FCSTD DOCUMENT  (FreeCAD 0.19R)
Label: drive_side_x-axis
License: All rights reserved
LicenseURL: http://en.wikipedia.org/wiki/All_rights_reserved
objects: App::Link×20, App::DocumentObjectGroup×3, PartDesign::CoordinateSystem×1, App::FeaturePython×1, App::Part×1
note: 1 computed .brp shape members not serialized (recipe doc carries the construction recipe); baked Part::Feature solids carry a one-line shape summary decoded from their .brp
EXTERNAL_REF file=angle_machined_2in_25_drive_side.FCStd obj=Local_CS010
EXTERNAL_REF file=bracket_nema_17.FCStd obj=Local_CS004
EXTERNAL_REF file=bracket_nema_17.FCStd obj=Body
EXTERNAL_REF file=bracket_nema_17.FCStd obj=Local_CS001
EXTERNAL_REF file=motor stepper 17hs4401s.FCStd obj=Local_CS
EXTERNAL_REF file=motor stepper 17hs4401s.FCStd obj=Body
EXTERNAL_REF file=coupling_8mm_5mm.FCStd obj=Local_CS
EXTERNAL_REF file=coupling_8mm_5mm.FCStd obj=Body
EXTERNAL_REF file=angle_machined_2in_25_drive_side.FCStd obj=Local_CS007
EXTERNAL_REF file=angle_machined_2in_25_drive_side.FCStd obj=Body
EXTERNAL_REF file=KFL08_bushing.FCStd obj=Local_CS001
EXTERNAL_REF file=KFL08_bushing.FCStd obj=Body
EXTERNAL_REF file=angle_machined_2in_25_drive_side.FCStd obj=Local_CS021
EXTERNAL_REF file=support_shaft_horiz_8mm.FCStd obj=Local_CS003
EXTERNAL_REF file=support_shaft_horiz_8mm.FCStd obj=Body
EXTERNAL_REF file=angle_machined_2in_25_drive_side.FCStd obj=Local_CS019
EXTERNAL_REF file=support_shaft_horiz_8mm.FCStd obj=Local_CS002
EXTERNAL_REF file=angle_machined_2in_25_drive_side.FCStd obj=Local_CS009
EXTERNAL_REF file=bearing_linear_8mm_horiz.FCStd obj=Local_CS
EXTERNAL_REF file=bearing_linear_8mm_horiz.FCStd obj=Body
EXTERNAL_REF file=angle_machined_2in_25_drive_side.FCStd obj=Local_CS
EXTERNAL_REF file=bearing_linear_8mm_horiz.FCStd obj=Local_CS004
EXTERNAL_REF file=shaft_8mm.FCStd obj=Local_CS
EXTERNAL_REF file=support_shaft_horiz_8mm.FCStd obj=Local_CS001
EXTERNAL_REF file=shaft_8mm.FCStd obj=Body
EXTERNAL_REF file=support_shaft_horiz_8mm.FCStd obj=Local_CS005
EXTERNAL_REF file=shaft_8mm.FCStd obj=Local_CS001
EXTERNAL_REF file=bearing_linear_8mm_horiz.FCStd obj=Local_CS003
EXTERNAL_REF file=bearing_linear_8mm_horiz.FCStd obj=Local_CS001
EXTERNAL_REF file=coupling_8mm_5mm.FCStd obj=Local_CS001
EXTERNAL_REF file=rod_threaded_8mm.FCStd obj=Local_CS001
EXTERNAL_REF file=rod_threaded_8mm.FCStd obj=Body
EXTERNAL_REF file=angle_machined_2in_25_drive_side.FCStd obj=Local_CS025
EXTERNAL_REF file=nut_angle.FCStd obj=Local_CS
EXTERNAL_REF file=nut_angle.FCStd obj=Body
EXTERNAL_REF file=nut_angle.FCStd obj=Local_CS001
EXTERNAL_REF file=nut_lead_screw_tr8x4.FCStd obj=Local_CS002
EXTERNAL_REF file=nut_lead_screw_tr8x4.FCStd obj=Body

FEATURE [App::DocumentObjectGroup] Parts
FEATURE [PartDesign::CoordinateSystem] LCS_Origin
  AttacherType = Attacher::AttachEngine3D
  MapMode = 2
  Support = -> [X_Axis]
FEATURE [App::FeaturePython] Variables  # WARN: FeaturePython — macro-defined, semantics opaque (R4)
  Type = App::PropertyContainer
FEATURE [App::DocumentObjectGroup] Constraints
FEATURE [App::DocumentObjectGroup] Configurations
FEATURE [App::Link] Body  label="bracket_nema_17"
  AttachedBy = #Local_CS004
  AttachedTo = Body003#Local_CS010
  AttachmentOffset = pos=(0,23,6.35) rot=(0,0,-1;4.71239rad)
  LinkPlacement = pos=(0.015,-4.15,-55.5) rot=(0,0,-1;3.14159rad)
  LinkedObject = -> <external bracket_nema_17.FCStd>#Body
  Placement = pos=(0.015,-4.15,-55.5) rot=(0,0,-1;3.14159rad)
  SolverId = Placement::ExpressionEngine
  expr: Placement = Body003.Placement * angle_machined_2in_25_drive_side#Local_CS010.Placement * AttachmentOffset * bracket_nema_17#Local_CS004.Placement ^ -1
FEATURE [App::Link] Body001  label="motor_nema"
  AttachedBy = #Local_CS
  AttachedTo = Body#Local_CS001
  AttachmentOffset = pos=(0,0,0) rot=(0.707107,0.707107,0;3.14159rad)
  LinkPlacement = pos=(0.015,0.35,-93.5) rot=(0,0,1;1.5708rad)
  LinkedObject = -> <external motor stepper 17hs4401s.FCStd>#Body
  Placement = pos=(0.015,0.35,-93.5) rot=(0,0,1;1.5708rad)
  SolverId = Placement::ExpressionEngine
  expr: Placement = Body.Placement * bracket_nema_17#Local_CS001.Placement * AttachmentOffset * motor_stepper_17hs4401s#Local_CS.Placement ^ -1
FEATURE [App::Link] Body002  label="coupling"
  AttachedBy = #Local_CS
  AttachedTo = Body001#Local_CS
  AttachmentOffset = pos=(0,0,-12) rot=(0,0,1;0rad)
  LinkPlacement = pos=(0.015,0.35,-31) rot=(0.707107,0.707107,0;3.14159rad)
  LinkedObject = -> <external coupling_8mm_5mm.FCStd>#Body
  Placement = pos=(0.015,0.35,-31) rot=(0.707107,0.707107,0;3.14159rad)
  SolverId = Placement::ExpressionEngine
  expr: Placement = Body001.Placement * motor_stepper_17hs4401s#Local_CS.Placement * AttachmentOffset * coupling_8mm_5mm#Local_CS.Placement ^ -1
FEATURE [App::Link] Body003  label="angle_machined_2in_25_drive"
  AttachedBy = #Local_CS007
  AttachedTo = Parent Assembly#LCS_Origin
  AttachmentOffset = pos=(0,0,0) rot=(0,1,0;3.14159rad)
  LinkPlacement = pos=(1.03e-14,-39,6.35) rot=(-0.707107,0,0.707107;3.14159rad)
  LinkedObject = -> <external angle_machined_2in_25_drive_side.FCStd>#Body
  Placement = pos=(1.03e-14,-39,6.35) rot=(-0.707107,0,0.707107;3.14159rad)
  SolverId = Placement::ExpressionEngine
  expr: Placement = LCS_Origin.Placement * AttachmentOffset * angle_machined_2in_25_drive_side#Local_CS007.Placement ^ -1
FEATURE [App::Link] Body004  label="bearing_axial1"
  AttachedBy = #Local_CS001
  AttachedTo = Body003#Local_CS007
  AttachmentOffset = pos=(0,0,0) rot=(0,0,1;3.14159rad)
  LinkPlacement = pos=(-3e-15,0,1.8e-15) rot=(0.707107,0.707107,0;3.14159rad)
  LinkedObject = -> <external KFL08_bushing.FCStd>#Body
  Placement = pos=(-3e-15,0,1.8e-15) rot=(0.707107,0.707107,0;3.14159rad)
  SolverId = Placement::ExpressionEngine
  expr: Placement = Body003.Placement * angle_machined_2in_25_drive_side#Local_CS007.Placement * AttachmentOffset * KFL08_bushing#Local_CS001.Placement ^ -1
FEATURE [App::Link] Body005  label="support_shaft_top"
  AttachedBy = #Local_CS003
  AttachedTo = Body003#Local_CS021
  AttachmentOffset = pos=(0,0,0) rot=(0.707107,0.707107,0;3.14159rad)
  LinkPlacement = pos=(40,-25,11.35) rot=(0,0,1;0rad)
  LinkedObject = -> <external support_shaft_horiz_8mm.FCStd>#Body
  Placement = pos=(40,-25,11.35) rot=(0,0,1;0rad)
  SolverId = Placement::ExpressionEngine
  expr: Placement = Body003.Placement * angle_machined_2in_25_drive_side#Local_CS021.Placement * AttachmentOffset * support_shaft_horiz_8mm#Local_CS003.Placement ^ -1
FEATURE [App::Link] Body006  label="support_shaft_other"
  AttachedBy = #Local_CS002
  AttachedTo = Body003#Local_CS019
  AttachmentOffset = pos=(0,0,0) rot=(0,0,1;1.5708rad)
  LinkPlacement = pos=(-40,-25,11.35) rot=(0,1,0;3.14159rad)
  LinkedObject = -> <external support_shaft_horiz_8mm.FCStd>#Body
  Placement = pos=(-40,-25,11.35) rot=(0,1,0;3.14159rad)
  SolverId = Placement::ExpressionEngine
  expr: Placement = Body003.Placement * angle_machined_2in_25_drive_side#Local_CS019.Placement * AttachmentOffset * support_shaft_horiz_8mm#Local_CS002.Placement ^ -1
FEATURE [App::Link] Body007  label="bearing_lin1"
  AttachedBy = #Local_CS
  AttachedTo = Body003#Local_CS009
  AttachmentOffset = pos=(0,0,0) rot=(0,1,0;3.14159rad)
  LinkPlacement = pos=(45,-50,-28.65) rot=(-0.57735,-0.57735,0.57735;4.18879rad)
  LinkedObject = -> <external bearing_linear_8mm_horiz.FCStd>#Body
  Placement = pos=(45,-50,-28.65) rot=(-0.57735,-0.57735,0.57735;4.18879rad)
  SolverId = Placement::ExpressionEngine
  expr: Placement = Body003.Placement * angle_machined_2in_25_drive_side#Local_CS009.Placement * AttachmentOffset * bearing_linear_8mm_horiz#Local_CS.Placement ^ -1
FEATURE [App::Link] bearing_lin2
  AttachedBy = #Local_CS004
  AttachedTo = Body003#Local_CS
  AttachmentOffset = pos=(0,0,0) rot=(1,0,0;3.14159rad)
  LinkPlacement = pos=(-45,-50,-28.65) rot=(-0.57735,0.57735,-0.57735;4.18879rad)
  LinkedObject = -> <external bearing_linear_8mm_horiz.FCStd>#Body
  Placement = pos=(-45,-50,-28.65) rot=(-0.57735,0.57735,-0.57735;4.18879rad)
  SolverId = Placement::ExpressionEngine
  expr: Placement = Body003.Placement * angle_machined_2in_25_drive_side#Local_CS.Placement * AttachmentOffset * bearing_linear_8mm_horiz#Local_CS004.Placement ^ -1
FEATURE [App::Link] Body008  label="shaft_upper"
  AttachedBy = #Local_CS
  AttachedTo = Body005#Local_CS001
  AttachmentOffset = pos=(0,0,0) rot=(-0.707107,-0.707107,0;3.14159rad)
  LinkPlacement = pos=(40,-25,406.35) rot=(-0.707107,0.707107,0;3.14159rad)
  LinkedObject = -> <external shaft_8mm.FCStd>#Body
  Placement = pos=(40,-25,406.35) rot=(-0.707107,0.707107,0;3.14159rad)
  SolverId = Placement::ExpressionEngine
  expr: Placement = Body005.Placement * support_shaft_horiz_8mm#Local_CS001.Placement * AttachmentOffset * shaft_8mm#Local_CS.Placement ^ -1
FEATURE [App::Link] upper_shaft  label="shaft_lower"
  AttachedBy = #Local_CS
  AttachedTo = Body006#Local_CS005
  LinkPlacement = pos=(-40,-25,406.35) rot=(0,1,0;3.14159rad)
  LinkedObject = -> <external shaft_8mm.FCStd>#Body
  Placement = pos=(-40,-25,406.35) rot=(0,1,0;3.14159rad)
  SolverId = Placement::ExpressionEngine
  expr: Placement = Body006.Placement * support_shaft_horiz_8mm#Local_CS005.Placement * AttachmentOffset * shaft_8mm#Local_CS.Placement ^ -1
FEATURE [App::Link] Body009
  AttachedBy = #Local_CS005
  AttachedTo = Body008#Local_CS001
  AttachmentOffset = pos=(0,0,0) rot=(0.707107,0.707107,0;3.14159rad)
  LinkPlacement = pos=(40,-25,401.35) rot=(0,0,1;0rad)
  LinkedObject = -> <external support_shaft_horiz_8mm.FCStd>#Body
  Placement = pos=(40,-25,401.35) rot=(0,0,1;0rad)
  SolverId = Placement::ExpressionEngine
  expr: Placement = Body008.Placement * shaft_8mm#Local_CS001.Placement * AttachmentOffset * support_shaft_horiz_8mm#Local_CS005.Placement ^ -1
FEATURE [App::Link] Body010
  AttachedBy = #Local_CS005
  AttachedTo = upper_shaft#Local_CS001
  AttachmentOffset = pos=(0,0,0) rot=(0,1,0;3.14159rad)
  LinkPlacement = pos=(-40,-25,401.35) rot=(0,0,1;3.14159rad)
  LinkedObject = -> <external support_shaft_horiz_8mm.FCStd>#Body
  Placement = pos=(-40,-25,401.35) rot=(0,0,1;3.14159rad)
  SolverId = Placement::ExpressionEngine
  expr: Placement = upper_shaft.Placement * shaft_8mm#Local_CS001.Placement * AttachmentOffset * support_shaft_horiz_8mm#Local_CS005.Placement ^ -1
FEATURE [App::Link] Body011
  AttachedBy = #Local_CS019
  AttachedTo = Body009#Local_CS002
  AttachmentOffset = pos=(0,0,0) rot=(0,0,1;4.71239rad)
  LinkPlacement = pos=(-1.705e-13,-39,406.35) rot=(-0.707107,0,-0.707107;3.14159rad)
  LinkedObject = -> <external angle_machined_2in_25_drive_side.FCStd>#Body
  Placement = pos=(-1.705e-13,-39,406.35) rot=(-0.707107,0,-0.707107;3.14159rad)
  SolverId = Placement::ExpressionEngine
  expr: Placement = Body009.Placement * support_shaft_horiz_8mm#Local_CS002.Placement * AttachmentOffset * angle_machined_2in_25_drive_side#Local_CS019.Placement ^ -1
FEATURE [App::Link] bearing_horiz_8_3
  AttachedBy = #Local_CS003
  AttachedTo = Body011#Local_CS
  AttachmentOffset = pos=(0,0,0) rot=(0,1,0;3.14159rad)
  LinkPlacement = pos=(45,-50,441.35) rot=(-0.57735,0.57735,-0.57735;4.18879rad)
  LinkedObject = -> <external bearing_linear_8mm_horiz.FCStd>#Body
  Placement = pos=(45,-50,441.35) rot=(-0.57735,0.57735,-0.57735;4.18879rad)
  SolverId = Placement::ExpressionEngine
  expr: Placement = Body011.Placement * angle_machined_2in_25_drive_side#Local_CS.Placement * AttachmentOffset * bearing_linear_8mm_horiz#Local_CS003.Placement ^ -1
FEATURE [App::Link] Body012
  AttachedBy = #Local_CS001
  AttachedTo = Body011#Local_CS009
  AttachmentOffset = pos=(0,0,0) rot=(1,0,0;3.14159rad)
  LinkPlacement = pos=(-45,-50,441.35) rot=(0.57735,0.57735,-0.57735;2.0944rad)
  LinkedObject = -> <external bearing_linear_8mm_horiz.FCStd>#Body
  Placement = pos=(-45,-50,441.35) rot=(0.57735,0.57735,-0.57735;2.0944rad)
  SolverId = Placement::ExpressionEngine
  expr: Placement = Body011.Placement * angle_machined_2in_25_drive_side#Local_CS009.Placement * AttachmentOffset * bearing_linear_8mm_horiz#Local_CS001.Placement ^ -1
FEATURE [App::Link] bearing_axial_2
  AttachedBy = #Local_CS001
  AttachedTo = Body011#Local_CS007
  LinkPlacement = pos=(-1.413e-13,7.82e-14,412.7) rot=(0,0,-1;1.5708rad)
  LinkedObject = -> <external KFL08_bushing.FCStd>#Body
  Placement = pos=(-1.413e-13,7.82e-14,412.7) rot=(0,0,-1;1.5708rad)
  SolverId = Placement::ExpressionEngine
  expr: Placement = Body011.Placement * angle_machined_2in_25_drive_side#Local_CS007.Placement * AttachmentOffset * KFL08_bushing#Local_CS001.Placement ^ -1
FEATURE [App::Link] Body013  label="Body"
  AttachedBy = #Local_CS001
  AttachedTo = Body002#Local_CS001
  AttachmentOffset = pos=(0,0,7) rot=(0,0,1;0rad)
  LinkPlacement = pos=(0.015,0.35,424.5) rot=(0.707107,0.707107,0;3.14159rad)
  LinkedObject = -> <external rod_threaded_8mm.FCStd>#Body
  Placement = pos=(0.015,0.35,424.5) rot=(0.707107,0.707107,0;3.14159rad)
  SolverId = Placement::ExpressionEngine
  expr: Placement = Body002.Placement * coupling_8mm_5mm#Local_CS001.Placement * AttachmentOffset * rod_threaded_8mm#Local_CS001.Placement ^ -1
FEATURE [App::Link] nut_angle_body
  AttachedBy = #Local_CS
  AttachedTo = Body003#Local_CS025
  AttachmentOffset = pos=(0,0,0) rot=(0,-1,0;3.14159rad)
  LinkPlacement = pos=(-5,-39,-4.15) rot=(0,-1,0;1.5708rad)
  LinkedObject = -> <external nut_angle.FCStd>#Body
  Placement = pos=(-5,-39,-4.15) rot=(0,-1,0;1.5708rad)
  SolverId = Placement::ExpressionEngine
  expr: Placement = Body003.Placement * angle_machined_2in_25_drive_side#Local_CS025.Placement * AttachmentOffset * nut_angle#Local_CS.Placement ^ -1
FEATURE [App::Link] nut_lead_screw_motor_side
  AttachedBy = #Local_CS002
  AttachedTo = nut_angle_body#Local_CS001
  AttachmentOffset = pos=(0,0,0) rot=(0.707107,-0.707107,0;3.14159rad)
  LinkPlacement = pos=(-5,-55.5,-4.15) rot=(0.357407,0.862856,0.357407;1.71777rad)
  LinkedObject = -> <external nut_lead_screw_tr8x4.FCStd>#Body
  Placement = pos=(-5,-55.5,-4.15) rot=(0.357407,0.862856,0.357407;1.71777rad)
  SolverId = Placement::ExpressionEngine
  expr: Placement = nut_angle_body.Placement * nut_angle#Local_CS001.Placement * AttachmentOffset * nut_lead_screw_tr8x4#Local_CS002.Placement ^ -1
FEATURE [App::Part] Assembly
  AssemblyType = Part::Link
  Group = -> [LCS_Origin,Variables,Constraints,Configurations,Body,Body001,Body002,Body003,Body004,Body005,Body006,Body007,bearing_lin2,Body008,upper_shaft,Body009,Body010,Body011,bearing_horiz_8_3,Body012,bearing_axial_2,Body013,nut_angle_body,nut_lead_screw_motor_side]
  LabelDocUser = drive_side_x-axis
  LabelPartUser = Assembly
  Origin = -> Origin
  Type = Assembly

RESOLVED EXTERNAL PARTS (link-assembly join: the EXTERNAL_REF files above that resolve inside this repo's crawl, each included once):
---- part KFL08_bushing.FCStd = doc fcstd_695011ae8dbb ----
FCSTD DOCUMENT  (FreeCAD 0.19R)
Label: KFL08_bushing
License: All rights reserved
LicenseURL: http://en.wikipedia.org/wiki/All_rights_reserved
objects: Sketcher::SketchObject×4, PartDesign::Pad×3, PartDesign::CoordinateSystem×2, PartDesign::Pocket×1, PartDesign::Body×1, Part::Feature×1
note: 16 computed .brp shape members not serialized (recipe doc carries the construction recipe); baked Part::Feature solids carry a one-line shape summary decoded from their .brp

FEATURE [Sketcher::SketchObject] Sketch
  FullyConstrained = true
  MapMode = 5
  Support = -> [XY_Plane]
  sketch-geometry (1):
    g0: Circle CenterX=0 CenterY=0 CenterZ=0 NormalX=0 NormalY=0 NormalZ=1 AngleXU=0 Radius=6
  constraints (2):
    c: Diameter(g0) = 12
    c: Coincident(g0,g-1)
FEATURE [PartDesign::Pad] Pad
  Direction = (1,1,1)
  Length = 12
  Length2 = 100
  Profile = -> Sketch
  Type = 0
FEATURE [Sketcher::SketchObject] Sketch001
  FullyConstrained = true
  MapMode = 5
  Support = -> [XY_Plane]
  sketch-geometry (11):
    g0: ArcOfCircle CenterX=0 CenterY=0 CenterZ=0 NormalX=0 NormalY=0 NormalZ=1 AngleXU=0 Radius=13.5 StartAngle=5.90541 EndAngle=6.66096
    g1: Circle CenterX=0 CenterY=18 CenterZ=0 NormalX=0 NormalY=0 NormalZ=1 AngleXU=0 Radius=2.5
    g2: Circle CenterX=0 CenterY=-18 CenterZ=0 NormalX=0 NormalY=0 NormalZ=1 AngleXU=0 Radius=2.5
    g3: LineSegment StartX=-5 StartY=24 StartZ=0 EndX=5 EndY=24 EndZ=0
    g4: LineSegment StartX=-5 StartY=-24 StartZ=0 EndX=5 EndY=-24 EndZ=0
    g5: GeomPoint X=-3e-16 Y=24 Z=0
    g6: LineSegment StartX=5 StartY=24 StartZ=0 EndX=12.5481 EndY=4.97957 EndZ=0
    g7: LineSegment StartX=-5 StartY=24 StartZ=0 EndX=-12.5481 EndY=4.97957 EndZ=0
    g8: LineSegment StartX=-5 StartY=-24 StartZ=0 EndX=-12.5481 EndY=-4.97959 EndZ=0
    g9: LineSegment StartX=5 StartY=-24 StartZ=0 EndX=12.5481 EndY=-4.97957 EndZ=0
    g10: ArcOfCircle CenterX=0 CenterY=0 CenterZ=0 NormalX=0 NormalY=0 NormalZ=1 AngleXU=0 Radius=13.5 StartAngle=2.76381 EndAngle=3.51937
  constraints (26):
    c: Coincident(g0,g-1)
    c: Diameter(g0) = 27  'L'
    c: Symmetric(g1,g2,g0)
    c: Vertical(g1,g0)
    c: DistanceY(g2,g1) = 36
    c: Horizontal(g3)
    c: Horizontal(g4)
    c: Vertical(g3,g4)
    c: Vertical(g3,g4)
    c: Symmetric(g3,g3,g5)
    c: DistanceX(g3,g3) = 10
    c: Coincident(g6,g3)
    c: Coincident(g7,g3)
    c: Coincident(g8,g4)
    c: Coincident(g9,g4)
    c: Tangent(g0,g9) = -1.5708
    c: Coincident(g10,g8) = 1.5708
    c: Equal(g0,g10)
    c: Tangent(g0,g6) = 1.5708
    c: Tangent(g10,g7) = -1.5708
    c: Coincident(g0,g10)
    c: Symmetric(g3,g4,g0)
    c: DistanceY(g4,g3) = 48
    c: Tangent(g8,g10)
    c: Diameter(g1) = 5
    c: Equal(g1,g2)
FEATURE [PartDesign::Pad] Pad001
  BaseFeature = -> Pad
  Direction = (1,1,1)
  Length = 4
  Length2 = 100
  Profile = -> Sketch001
  Type = 0
FEATURE [Sketcher::SketchObject] Sketch002
  ExternalGeometry = -> [Pad001]
  FullyConstrained = true
  MapMode = 5
  Support = -> [XY_Plane]
  sketch-geometry (2):
    g0: Circle CenterX=0 CenterY=0 CenterZ=0 NormalX=0 NormalY=0 NormalZ=1 AngleXU=0 Radius=13.5
    g1: GeomPoint X=12.5481 Y=-4.97957 Z=0
  constraints (3):
    c: Coincident(g0,g-1)
    c: PointOnObject(g1,g0)
    c: Coincident(g-3,g1)
FEATURE [PartDesign::Pad] Pad002
  BaseFeature = -> Pad001
  Direction = (1,1,1)
  Length = 8.5
  Length2 = 100
  Profile = -> Sketch002
  Type = 0
FEATURE [Sketcher::SketchObject] Sketch003
  FullyConstrained = true
  MapMode = 5
  Support = -> [XY_Plane]
  sketch-geometry (1):
    g0: Circle CenterX=0 CenterY=0 CenterZ=0 NormalX=0 NormalY=0 NormalZ=1 AngleXU=0 Radius=4
  constraints (2):
    c: Coincident(g0,g-1)
    c: Diameter(g0) = 8
FEATURE [PartDesign::Pocket] Pocket
  BaseFeature = -> Pad002
  Length = 5
  Length2 = 100
  Midplane = true
  Profile = -> Sketch003
  Refine = true
  Type = 1
FEATURE [PartDesign::CoordinateSystem] Local_CS
  AttacherType = Attacher::AttachEngine3D
  MapMode = 11
  Placement = pos=(0,0,12) rot=(0,0,1;1.5708rad)
  Support = -> [Pocket]
FEATURE [PartDesign::CoordinateSystem] Local_CS001
  AttacherType = Attacher::AttachEngine3D
  MapMode = 11
  Placement = pos=(0,0,0) rot=(0,0,1;1.5708rad)
  Support = -> [Pocket]
FEATURE [PartDesign::Body] Body
  Group = -> [Sketch,Pad,Sketch001,Pad001,Sketch002,Pad002,Sketch003,Pocket,Local_CS,Local_CS001]
  Origin = -> Origin
  Tip = -> Pocket
FEATURE [Part::Feature] Pocket_cs
---- part angle_machined_2in_25_drive_side.FCStd = doc fcstd_0c68a8f2e488 ----
FCSTD DOCUMENT  (FreeCAD 0.19R)
Label: angle_machined_2in_25_drive_side
License: All rights reserved
LicenseURL: http://en.wikipedia.org/wiki/All_rights_reserved
objects: TechDraw::DrawViewDimension×26, PartDesign::CoordinateSystem×17, Sketcher::SketchObject×9, PartDesign::Pocket×7, PartDesign::Mirrored×3, TechDraw::DrawViewPart×3, PartDesign::Pad×2, PartDesign::Fillet×1, PartDesign::LinearPattern×1, PartDesign::Hole×1, PartDesign::Body×1, TechDraw::DrawSVGTemplate×1, TechDraw::DrawViewAnnotation×1, TechDraw::DrawPage×1
note: 53 computed .brp shape members not serialized (recipe doc carries the construction recipe); baked Part::Feature solids carry a one-line shape summary decoded from their .brp

FEATURE [Sketcher::SketchObject] Sketch
  FullyConstrained = true
  MapMode = 5
  Support = -> [XY_Plane]
  sketch-geometry (6):
    g0: LineSegment StartX=0 StartY=0 StartZ=0 EndX=50.8 EndY=0 EndZ=0
    g1: LineSegment StartX=50.8 StartY=0 StartZ=0 EndX=50.8 EndY=-6.35 EndZ=0
    g2: LineSegment StartX=50.8 StartY=-6.35 StartZ=0 EndX=6.35 EndY=-6.35 EndZ=0
    g3: LineSegment StartX=6.35 StartY=-6.35 StartZ=0 EndX=6.35 EndY=-50.8 EndZ=0
    g4: LineSegment StartX=6.35 StartY=-50.8 StartZ=0 EndX=0 EndY=-50.8 EndZ=0
    g5: LineSegment StartX=0 StartY=-50.8 StartZ=0 EndX=0 EndY=0 EndZ=0
  constraints (17):
    c: Coincident(g-1,g0)
    c: PointOnObject(g0,g-1)
    c: Coincident(g0,g1)
    c: Vertical(g1)
    c: Coincident(g1,g2)
    c: Horizontal(g2)
    c: Coincident(g2,g3)
    c: Vertical(g3)
    c: Coincident(g3,g4)
    c: PointOnObject(g4,g-2)
    c: Horizontal(g4)
    c: Coincident(g4,g5)
    c: Coincident(g5,g0)
    c: Equal(g1,g4)
    c: DistanceY(g1,g1) = 6.35
    c: DistanceX(g0,g0) = 50.8
    c: Equal(g0,g5)
FEATURE [PartDesign::Pad] Pad
  Direction = (1,1,1)
  Length = 62
  Length2 = 100
  Profile = -> Sketch
  Refine = true
  Reversed = true
  Type = 0
FEATURE [Sketcher::SketchObject] Sketch001
  FullyConstrained = true
  MapMode = 5
  Placement = pos=(0,0,0) rot=(0.57735,0.57735,0.57735;2.0944rad)
  Support = -> [YZ_Plane]
  sketch-geometry (3):
    g0: Circle CenterX=-14 CenterY=-40 CenterZ=0 NormalX=0 NormalY=0 NormalZ=1 AngleXU=0 Radius=6.35
    g1: Circle CenterX=-14 CenterY=-24 CenterZ=0 NormalX=0 NormalY=0 NormalZ=1 AngleXU=0 Radius=2.5
    g2: Circle CenterX=-14 CenterY=-56 CenterZ=0 NormalX=0 NormalY=0 NormalZ=1 AngleXU=0 Radius=2.5
  constraints (8):
    c: Diameter(g0) = 12.7
    c: Diameter(g1) = 5
    c: Equal(g1,g2)
    c: Symmetric(g1,g2,g0)
    c: Vertical(g1,g0)
    c: Distance(g1,g2) = 32
    c: DistanceX(g0,g-1) = 14
    c: DistanceY(g0,g-1) = 40
FEATURE [Sketcher::SketchObject] Sketch002
  FullyConstrained = true
  MapMode = 5
  Placement = pos=(0,0,0) rot=(0.57735,0.57735,0.57735;2.0944rad)
  Support = -> [YZ_Plane]
  sketch-geometry (3):
    g0: Circle CenterX=-39 CenterY=0 CenterZ=0 NormalX=0 NormalY=0 NormalZ=1 AngleXU=0 Radius=5.35781
    g1: Circle CenterX=-39 CenterY=18 CenterZ=0 NormalX=0 NormalY=0 NormalZ=1 AngleXU=0 Radius=2.5
    g2: Circle CenterX=-39 CenterY=-18 CenterZ=0 NormalX=0 NormalY=0 NormalZ=1 AngleXU=0 Radius=2.5
  constraints (8):
    c: Diameter(g0) = 10.7156
    c: Horizontal(g0,g-1)
    c: Vertical(g1,g0)
    c: Diameter(g1) = 5
    c: Equal(g1,g2)
    c: Symmetric(g1,g2,g0)
    c: DistanceY(g2,g1) = 36
    c: DistanceX(g1,g-1) = 39
FEATURE [Sketcher::SketchObject] Sketch003
  FullyConstrained = true
  MapMode = 5
  Placement = pos=(0,0,0) rot=(1,0,0;1.5708rad)
  Support = -> [XZ_Plane]
  sketch-geometry (4):
    g0: LineSegment StartX=6.35 StartY=251.119 StartZ=0 EndX=66.35 EndY=251.119 EndZ=0
    g1: LineSegment StartX=66.35 StartY=251.119 StartZ=0 EndX=66.35 EndY=200 EndZ=0
    g2: LineSegment StartX=66.35 StartY=200 StartZ=0 EndX=6.35 EndY=200 EndZ=0
    g3: LineSegment StartX=6.35 StartY=200 StartZ=0 EndX=6.35 EndY=251.119 EndZ=0
  constraints (12):
    c: Coincident(g0,g1)
    c: Coincident(g1,g2)
    c: Coincident(g2,g3)
    c: Coincident(g3,g0)
    c: Horizontal(g0)
    c: Horizontal(g2)
    c: Vertical(g1)
    c: Vertical(g3)
    c: DistanceY(g3,g3) = 51.1187
    c: DistanceY(g-1,g2) = 200
    c: DistanceX(g0,g0) = 60
    c: DistanceX(g-1,g0) = 6.35
FEATURE [Sketcher::SketchObject] Sketch004
  FullyConstrained = true
  MapMode = 5
  Placement = pos=(0,0,0) rot=(1,0,0;1.5708rad)
  Support = -> [XZ_Plane]
  sketch-geometry (7):
    g0: Circle CenterX=45 CenterY=15 CenterZ=0 NormalX=0 NormalY=0 NormalZ=1 AngleXU=0 Radius=1.865
    g1: Circle CenterX=45 CenterY=-15 CenterZ=0 NormalX=0 NormalY=0 NormalZ=1 AngleXU=0 Radius=1.865
    g2: Circle CenterX=23 CenterY=15 CenterZ=0 NormalX=0 NormalY=0 NormalZ=1 AngleXU=0 Radius=1.865
    g3: Circle CenterX=23 CenterY=-15 CenterZ=0 NormalX=0 NormalY=0 NormalZ=1 AngleXU=0 Radius=1.865
    g4: LineSegment StartX=0 StartY=0 StartZ=0 EndX=-20.31 EndY=0 EndZ=0
    g5: LineSegment StartX=34 StartY=0 StartZ=0 EndX=34 EndY=70 EndZ=0
    g6: Circle CenterX=34 CenterY=0 CenterZ=0 NormalX=0 NormalY=0 NormalZ=1 AngleXU=0 Radius=0.05
  constraints (18):
    c: Horizontal(g4)
    c: Coincident(g4,g-1)
    c: Distance(g4) = 20.31
    c: Vertical(g5)
    c: Horizontal(g5,g-1)
    c: Symmetric(g2,g0,g5)
    c: Symmetric(g2,g3,g4)
    c: Symmetric(g0,g1,g4)
    c: DistanceX(g2,g0) = 22
    c: Equal(g2,g0)
    c: Equal(g1,g0)
    c: Equal(g1,g3)
    c: Diameter(g0) = 3.73
    c: DistanceY(g1,g0) = 30
    c: DistanceX(g-1,g5) = 34  'motor_x'
    c: DistanceY(g5,g5) = 70
    c: Coincident(g6,g5)
    c: Diameter(g6) = 0.1
FEATURE [PartDesign::Pad] Pad001
  BaseFeature = -> Pad
  Direction = (1,1,1)
  Length = 62
  Length2 = 100
  Profile = -> Sketch
  Refine = true
  Type = 0
FEATURE [PartDesign::Fillet] Fillet
  Base = -> Pad001 [Edge17,Edge18,Edge16]
  BaseFeature = -> Pad001
  Radius = 4.5
  Refine = true
  SupportTransform = false
FEATURE [PartDesign::Pocket] Pocket  label="top_bearing"
  BaseFeature = -> Fillet
  Length = 20
  Length2 = 100
  Profile = -> Sketch001
  Refine = true
  Reversed = true
  Type = 1
FEATURE [PartDesign::LinearPattern] LinearPattern  label="LinearPattern_lower_bearing"
  BaseFeature = -> Pocket
  Direction = -> Sketch001 [V_Axis]
  Length = 80
  Occurrences = 2
  Originals = -> [Pocket]
  Refine = true
FEATURE [PartDesign::Pocket] Pocket001  label="drive_hole_clearance"
  BaseFeature = -> LinearPattern
  Length = 5
  Length2 = 100
  Midplane = true
  Profile = -> Sketch002
  Refine = true
  Reversed = true
  Type = 1
FEATURE [PartDesign::Pocket] Pocket002  label="gross_cut"
  BaseFeature = -> Pocket001
  Length = 5
  Length2 = 100
  Midplane = true
  Profile = -> Sketch003
  Refine = true
  Type = 1
FEATURE [PartDesign::Mirrored] Mirrored001
  BaseFeature = -> Pocket002
  MirrorPlane = -> Sketch003 [H_Axis]
  Originals = -> [Pocket002]
  Refine = true
FEATURE [PartDesign::Pocket] Pocket003
  BaseFeature = -> Mirrored001
  Length = 5
  Length2 = 100
  Midplane = true
  Profile = -> Sketch004
  Type = 1
FEATURE [Sketcher::SketchObject] Sketch005
  FullyConstrained = true
  MapMode = 5
  Support = -> [XY_Plane]
  sketch-geometry (4):
    g0: LineSegment StartX=6.35 StartY=-6 StartZ=0 EndX=66.35 EndY=-6 EndZ=0
    g1: LineSegment StartX=66.35 StartY=-6 StartZ=0 EndX=66.35 EndY=-18.25 EndZ=0
    g2: LineSegment StartX=66.35 StartY=-18.25 StartZ=0 EndX=6.35 EndY=-18.25 EndZ=0
    g3: LineSegment StartX=6.35 StartY=-18.25 StartZ=0 EndX=6.35 EndY=-6 EndZ=0
  constraints (12):
    c: Coincident(g0,g1)
    c: Coincident(g1,g2)
    c: Coincident(g2,g3)
    c: Coincident(g3,g0)
    c: Horizontal(g0)
    c: Horizontal(g2)
    c: Vertical(g1)
    c: Vertical(g3)
    c: DistanceY(g1,g1) = 12.25
    c: DistanceX(g0,g0) = 60
    c: DistanceX(g-1,g0) = 6.35
    c: DistanceY(g0,g-1) = 6
FEATURE [PartDesign::Pocket] Pocket004
  BaseFeature = -> Pocket003
  Length = 5
  Length2 = 100
  Midplane = true
  Profile = -> Sketch005
  Refine = true
  Type = 1
FEATURE [Sketcher::SketchObject] Sketch006
  FullyConstrained = true
  MapMode = 5
  Placement = pos=(0,0,0) rot=(0.57735,0.57735,0.57735;2.0944rad)
  Support = -> [YZ_Plane]
  sketch-geometry (4):
    g0: LineSegment StartX=-62.1666 StartY=69.7638 StartZ=0 EndX=-24.8 EndY=69.7638 EndZ=0
    g1: LineSegment StartX=-24.8 StartY=69.7638 StartZ=0 EndX=-24.8 EndY=25 EndZ=0
    g2: LineSegment StartX=-24.8 StartY=25 StartZ=0 EndX=-62.1666 EndY=25 EndZ=0
    g3: LineSegment StartX=-62.1666 StartY=25 StartZ=0 EndX=-62.1666 EndY=69.7638 EndZ=0
  constraints (12):
    c: Coincident(g0,g1)
    c: Coincident(g1,g2)
    c: Coincident(g2,g3)
    c: Coincident(g3,g0)
    c: Horizontal(g0)
    c: Horizontal(g2)
    c: Vertical(g1)
    c: Vertical(g3)
    c: DistanceX(g0,g-1) = 24.8
    c: DistanceY(g-1,g1) = 25
    c: DistanceX(g2,g2) = 37.3666
    c: DistanceY(g3,g3) = 44.7638
FEATURE [PartDesign::Pocket] Pocket005
  BaseFeature = -> Pocket004
  Length = 5
  Length2 = 100
  Midplane = true
  Profile = -> Sketch006
  Refine = true
  Type = 1
FEATURE [PartDesign::Mirrored] Mirrored
  BaseFeature = -> Pocket005
  MirrorPlane = -> Sketch006 [H_Axis]
  Originals = -> [Pocket005]
  Refine = true
FEATURE [PartDesign::CoordinateSystem] Local_CS007  label="lcs_NUT"
  AttacherType = Attacher::AttachEngine3D
  MapMode = 11
  Placement = pos=(6.35,-39,1.81e-14) rot=(0.707107,0,0.707107;3.14159rad)
  Support = -> [Mirrored]
FEATURE [Sketcher::SketchObject] Sketch007
  FullyConstrained = true
  MapMode = 5
  Placement = pos=(0,0,0) rot=(1,0,0;1.5708rad)
  Support = -> [XZ_Plane]
  sketch-geometry (5):
    g0: Circle CenterX=23 CenterY=54 CenterZ=0 NormalX=0 NormalY=0 NormalZ=1 AngleXU=0 Radius=2.5
    g1: Circle CenterX=47 CenterY=54 CenterZ=0 NormalX=0 NormalY=0 NormalZ=1 AngleXU=0 Radius=2.5
    g2: Circle CenterX=47 CenterY=36 CenterZ=0 NormalX=0 NormalY=0 NormalZ=1 AngleXU=0 Radius=2.5
    g3: Circle CenterX=23 CenterY=36 CenterZ=0 NormalX=0 NormalY=0 NormalZ=1 AngleXU=0 Radius=2.5
    g4: GeomPoint X=35 Y=45 Z=0
  constraints (13):
    c: Vertical(g0,g3)
    c: Horizontal(g1,g0)
    c: Horizontal(g2,g3)
    c: Vertical(g2,g1)
    c: DistanceX(g0,g1) = 24
    c: DistanceY(g2,g1) = 18
    c: Equal(g1,g2)
    c: Equal(g2,g3)
    c: Equal(g3,g0)
    c: Diameter(g1) = 5
    c: Symmetric(g3,g1,g4)
    c: DistanceY(g-1,g4) = 45  'y1'
    c: DistanceX(g-1,g4) = 35  'x1'
FEATURE [PartDesign::Pocket] Pocket006  label="bearing_holes"
  BaseFeature = -> Mirrored
  Length = 5
  Length2 = 100
  Midplane = true
  Profile = -> Sketch007
  Refine = true
  Type = 1
FEATURE [PartDesign::Mirrored] Mirrored002
  BaseFeature = -> Pocket006
  MirrorPlane = -> Sketch007 [H_Axis]
  Originals = -> [Pocket006]
  Refine = true
FEATURE [PartDesign::CoordinateSystem] Local_CS
  AttacherType = Attacher::AttachEngine3D
  MapMode = 11
  Placement = pos=(47,0,54) rot=(0.57735,-0.57735,0.57735;2.0944rad)
  Support = -> [Mirrored002]
FEATURE [PartDesign::CoordinateSystem] Local_CS009
  AttacherType = Attacher::AttachEngine3D
  MapMode = 11
  Placement = pos=(23,0,-36) rot=(0.57735,-0.57735,0.57735;2.0944rad)
  Support = -> [Mirrored002]
FEATURE [PartDesign::CoordinateSystem] Local_CS010
  AttacherType = Attacher::AttachEngine3D
  MapMode = 11
  Placement = pos=(45,0,15) rot=(0.57735,-0.57735,0.57735;2.0944rad)
  Support = -> [Mirrored002]
FEATURE [PartDesign::CoordinateSystem] Local_CS011
  AttacherType = Attacher::AttachEngine3D
  MapMode = 11
  Placement = pos=(23,3.3e-15,-15) rot=(0.57735,-0.57735,0.57735;2.0944rad)
  Support = -> [Sketch004]
FEATURE [PartDesign::CoordinateSystem] Local_CS012
  AttacherType = Attacher::AttachEngine3D
  MapMode = 11
  Placement = pos=(47,0,-54) rot=(0.57735,-0.57735,0.57735;2.0944rad)
  Support = -> [Mirrored002]
FEATURE [PartDesign::CoordinateSystem] Local_CS013
  AttacherType = Attacher::AttachEngine3D
  MapMode = 11
  Placement = pos=(23,0,15) rot=(0.57735,-0.57735,0.57735;2.0944rad)
  Support = -> [Mirrored002]
FEATURE [PartDesign::CoordinateSystem] Local_CS015
  AttacherType = Attacher::AttachEngine3D
  MapMode = 11
  Placement = pos=(6.35,-14,56) rot=(0.707107,0,-0.707107;3.14159rad)
  Support = -> [Mirrored002]
FEATURE [PartDesign::CoordinateSystem] Local_CS016
  AttacherType = Attacher::AttachEngine3D
  MapMode = 11
  Placement = pos=(6.35,-14,24) rot=(0.707107,0,-0.707107;3.14159rad)
  Support = -> [Mirrored002]
FEATURE [PartDesign::CoordinateSystem] Local_CS017
  AttacherType = Attacher::AttachEngine3D
  MapMode = 11
  Placement = pos=(6.35,-14,-24) rot=(0.707107,0,-0.707107;3.14159rad)
  Support = -> [Mirrored002]
FEATURE [PartDesign::CoordinateSystem] Local_CS018
  AttacherType = Attacher::AttachEngine3D
  MapMode = 11
  Placement = pos=(6.35,-14,-56) rot=(0.707107,0,-0.707107;3.14159rad)
  Support = -> [Mirrored002]
FEATURE [PartDesign::CoordinateSystem] Local_CS019
  AttacherType = Attacher::AttachEngine3D
  MapMode = 11
  Placement = pos=(-1.8e-14,-14,56) rot=(0.707107,0,0.707107;3.14159rad)
  Support = -> [Mirrored002]
FEATURE [PartDesign::CoordinateSystem] Local_CS020
  AttacherType = Attacher::AttachEngine3D
  MapMode = 11
  Placement = pos=(-1.8e-14,-14,24) rot=(0.707107,0,0.707107;3.14159rad)
  Support = -> [Mirrored002]
FEATURE [PartDesign::CoordinateSystem] Local_CS021
  AttacherType = Attacher::AttachEngine3D
  MapMode = 11
  Placement = pos=(0,-14,-24) rot=(0.707107,0,0.707107;3.14159rad)
  Support = -> [Mirrored002]
FEATURE [PartDesign::CoordinateSystem] Local_CS022
  AttacherType = Attacher::AttachEngine3D
  MapMode = 11
  Placement = pos=(0,-14,-56) rot=(0.707107,0,0.707107;3.14159rad)
  Support = -> [Mirrored002]
FEATURE [Sketcher::SketchObject] Sketch008
  FullyConstrained = true
  MapMode = 5
  Placement = pos=(0,0,0) rot=(0,0.707107,0.707107;3.14159rad)
  Support = -> [Mirrored002]
  sketch-geometry (8):
    g0: Circle CenterX=-18 CenterY=-7.5 CenterZ=0 NormalX=0 NormalY=0 NormalZ=1 AngleXU=0 Radius=1
    g1: Circle CenterX=-3 CenterY=-7.5 CenterZ=0 NormalX=0 NormalY=0 NormalZ=1 AngleXU=0 Radius=1
    g2: Circle CenterX=-3 CenterY=-22.5 CenterZ=0 NormalX=0 NormalY=0 NormalZ=1 AngleXU=0 Radius=1
    g3: Circle CenterX=-18 CenterY=-22.5 CenterZ=0 NormalX=0 NormalY=0 NormalZ=1 AngleXU=0 Radius=1
    g4: Circle CenterX=-3 CenterY=7.5 CenterZ=0 NormalX=0 NormalY=0 NormalZ=1 AngleXU=0 Radius=1
    g5: Circle CenterX=-3 CenterY=22.5 CenterZ=0 NormalX=0 NormalY=0 NormalZ=1 AngleXU=0 Radius=1
    g6: Circle CenterX=-18 CenterY=22.5 CenterZ=0 NormalX=0 NormalY=0 NormalZ=1 AngleXU=0 Radius=1
    g7: Circle CenterX=-18 CenterY=7.5 CenterZ=0 NormalX=0 NormalY=0 NormalZ=1 AngleXU=0 Radius=1
  constraints (20):
    c: Equal(g2,g1)
    c: Equal(g0,g1)
    c: Equal(g3,g0)
    c: DistanceX(g3,g2) = 15
    c: DistanceY(g2,g1) = 15
    c: Horizontal(g2,g3)
    c: Diameter(g0) = 2
    c: DistanceX(g1,g-1) = 3
    c: Horizontal(g1,g0)
    c: Vertical(g3,g0)
    c: Vertical(g1,g2)
    c: DistanceY(g1,g-1) = 7.5
    c: Symmetric(g1,g4,g-1)
    c: Symmetric(g0,g7,g-1)
    c: Symmetric(g2,g5,g-1)
    c: Symmetric(g6,g3,g-1)
    c: Equal(g4,g7)
    c: Equal(g5,g4)
    c: Equal(g5,g6)
    c: Equal(g3,g6)
FEATURE [PartDesign::Hole] Hole
  BaseFeature = -> Mirrored002
  Depth = 10
  DepthType = 0
  Diameter = 2.5
  DrillForDepth = false
  DrillPoint = 1
  DrillPointAngle = 118
  HoleCutCountersinkAngle = 90
  HoleCutCustomValues = false
  HoleCutDepth = 3.4
  HoleCutDiameter = 6.1
  HoleCutType = 0
  ModelActualThread = false
  Profile = -> Sketch008
  Refine = true
  Tapered = false
  TaperedAngle = 90
  ThreadAngle = 60
  ThreadClass = 0
  ThreadCutOffInner = 0.0541266
  ThreadCutOffOuter = 0.108253
  ThreadDirection = 0
  ThreadFit = 1
  ThreadPitch = 0.5
  ThreadSize = 9
  ThreadType = 1
  Threaded = true
FEATURE [PartDesign::CoordinateSystem] Local_CS023
  AttacherType = Attacher::AttachEngine3D
  MapMode = 5
  Placement = pos=(0,0,0) rot=(0,0.707107,0.707107;3.14159rad)
  Support = -> [Hole]
FEATURE [PartDesign::CoordinateSystem] Local_CS025
  AttacherType = Attacher::AttachEngine3D
  MapMode = 11
  Placement = pos=(3,-5e-15,-22.5) rot=(0.57735,-0.57735,-0.57735;4.18879rad)
  Support = -> [Hole]
FEATURE [PartDesign::Body] Body
  Group = -> [Sketch,Pad,Pad001,Sketch001,Fillet,Pocket,Sketch002,LinearPattern,Pocket001,Sketch003,Pocket002,Mirrored001,Sketch004,Pocket003,Sketch005,Pocket004,Sketch006,Pocket005,Mirrored,Local_CS007,Sketch007,Pocket006,Mirrored002,Local_CS,Local_CS009,Local_CS010,Local_CS011,Local_CS012,Local_CS013,Local_CS015,Local_CS016,Local_CS017,Local_CS018,Local_CS019,Local_CS020,Local_CS021,Local_CS022,Sketch008,+3 more]
  Origin = -> Origin
  Tip = -> Hole
FEATURE [TechDraw::DrawSVGTemplate] Template
  EditableTexts = 1 : 4=1:2; 99=1; 99 - MM=1; DRAWING NO.=DRAWING NO.; Titel / zusätzliche Informationen=test; YYYY-MM-DD=2020-10-06
  Height = 210
  Orientation = 1
  Width = 297
FEATURE [TechDraw::DrawViewPart] View  label=" "
  CoarseView = false
  Direction = (0,1,0)
  Focus = 100
  HardHidden = false
  IsoCount = 0
  IsoHidden = false
  IsoVisible = false
  LockPosition = true
  Perspective = false
  Rotation = 0
  Scale = 0.5
  ScaleType = 0
  SeamHidden = false
  SeamVisible = true
  SmoothHidden = false
  SmoothVisible = true
  Source = -> [Body]
  X = 134.439
  XDirection = (-1,0,0)
  Y = 108
FEATURE [TechDraw::DrawViewDimension] Dimension
  Arbitrary = false
  ArbitraryTolerances = false
  EqualTolerance = true
  FormatSpec = %.0f
  FormatSpecOverTolerance = %+.0f
  FormatSpecUnderTolerance = %+.0f
  Inverted = false
  LockPosition = false
  MeasureType = 1
  OverTolerance = 0
  References2D = -> [View]
  Rotation = 0
  Scale = 0.5
  ScaleType = 0
  TheoreticalExact = false
  Type = 1
  UnderTolerance = 0
  X = 8.68058
  Y = 60.3564
FEATURE [TechDraw::DrawViewDimension] Dimension002
  Arbitrary = false
  ArbitraryTolerances = false
  EqualTolerance = true
  FormatSpec = %.0f
  FormatSpecOverTolerance = %+.0f
  FormatSpecUnderTolerance = %+.0f
  Inverted = false
  LockPosition = false
  MeasureType = 1
  OverTolerance = 0
  References2D = -> [View]
  Rotation = 0
  Scale = 0.5
  ScaleType = 0
  TheoreticalExact = false
  Type = 2
  UnderTolerance = 0
  X = -65.2145
  Y = 0.08206
FEATURE [TechDraw::DrawViewDimension] Dimension003
  Arbitrary = false
  ArbitraryTolerances = false
  EqualTolerance = true
  FormatSpec = %.0f
  FormatSpecOverTolerance = %+.0f
  FormatSpecUnderTolerance = %+.0f
  Inverted = false
  LockPosition = false
  MeasureType = 1
  OverTolerance = 0
  References2D = -> [View]
  Rotation = 0
  Scale = 0.5
  ScaleType = 0
  TheoreticalExact = false
  Type = 2
  UnderTolerance = 0
  X = -27.5176
  Y = 41.8447
FEATURE [TechDraw::DrawViewPart] View001
  CoarseView = false
  Direction = (-0.577,0.577,0.577)
  Focus = 100
  HardHidden = false
  IsoCount = 0
  IsoHidden = false
  IsoVisible = false
  LockPosition = false
  Perspective = false
  Rotation = 0
  Scale = 0.5
  ScaleType = 0
  SeamHidden = false
  SeamVisible = true
  SmoothHidden = false
  SmoothVisible = true
  Source = -> [Body]
  X = 36.4593
  XDirection = (-0.707,-0.707,0)
  Y = 151.571
FEATURE [TechDraw::DrawViewPart] View002  label="  "
  CoarseView = false
  Direction = (-1,0,0)
  Focus = 100
  HardHidden = false
  IsoCount = 0
  IsoHidden = false
  IsoVisible = false
  LockPosition = true
  Perspective = false
  Rotation = 0
  Scale = 0.5
  ScaleType = 0
  SeamHidden = false
  SeamVisible = true
  SmoothHidden = false
  SmoothVisible = true
  Source = -> [Body]
  X = 220
  XDirection = (0,-1,0)
  Y = 108
FEATURE [TechDraw::DrawViewDimension] Dimension004
  Arbitrary = false
  ArbitraryTolerances = false
  EqualTolerance = true
  FormatSpec = %.0f
  FormatSpecOverTolerance = %+.0f
  FormatSpecUnderTolerance = %+.0f
  Inverted = false
  LockPosition = false
  MeasureType = 1
  OverTolerance = 0
  References2D = -> [View]
  Rotation = 0
  Scale = 0.5
  ScaleType = 0
  TheoreticalExact = false
  Type = 2
  UnderTolerance = 0
  X = -36.0722
  Y = 15.3836
FEATURE [TechDraw::DrawViewDimension] Dimension005
  Arbitrary = false
  ArbitraryTolerances = false
  EqualTolerance = true
  FormatSpec = ⌀%.0f
  FormatSpecOverTolerance = %+.0f
  FormatSpecUnderTolerance = %+.0f
  Inverted = false
  LockPosition = false
  MeasureType = 1
  OverTolerance = 0
  References2D = -> [View]
  Rotation = 0
  Scale = 0.5
  ScaleType = 0
  TheoreticalExact = false
  Type = 5
  UnderTolerance = 0
  X = 7.8661
  Y = 39.6018
FEATURE [TechDraw::DrawViewDimension] Dimension006
  Arbitrary = false
  ArbitraryTolerances = false
  EqualTolerance = true
  FormatSpec = %.0f
  FormatSpecOverTolerance = %+.0f
  FormatSpecUnderTolerance = %+.0f
  Inverted = false
  LockPosition = false
  MeasureType = 1
  OverTolerance = 0
  References2D = -> [View]
  Rotation = 0
  Scale = 0.5
  ScaleType = 0
  TheoreticalExact = false
  Type = 2
  UnderTolerance = 0
  X = -30.8384
  Y = -7.25973
FEATURE [TechDraw::DrawViewDimension] Dimension007
  Arbitrary = false
  ArbitraryTolerances = false
  EqualTolerance = true
  FormatSpec = %.0f
  FormatSpecOverTolerance = %+.0f
  FormatSpecUnderTolerance = %+.0f
  Inverted = false
  LockPosition = false
  MeasureType = 1
  OverTolerance = 0
  References2D = -> [View]
  Rotation = 0
  Scale = 0.5
  ScaleType = 0
  TheoreticalExact = false
  Type = 2
  UnderTolerance = 0
  X = 38.0639
  Y = 20.3537
FEATURE [TechDraw::DrawViewDimension] Dimension008
  Arbitrary = false
  ArbitraryTolerances = false
  EqualTolerance = true
  FormatSpec = %.0f
  FormatSpecOverTolerance = %+.0f
  FormatSpecUnderTolerance = %+.0f
  Inverted = false
  LockPosition = false
  MeasureType = 1
  OverTolerance = 0
  References2D = -> [View]
  Rotation = 0
  Scale = 0.5
  ScaleType = 0
  TheoreticalExact = false
  Type = 1
  UnderTolerance = 0
  X = 25.4362
  Y = 18.7897
FEATURE [TechDraw::DrawViewDimension] Dimension010
  Arbitrary = false
  ArbitraryTolerances = false
  EqualTolerance = true
  FormatSpec = ⌀%.0f
  FormatSpecOverTolerance = %+.0f
  FormatSpecUnderTolerance = %+.0f
  Inverted = false
  LockPosition = false
  MeasureType = 1
  OverTolerance = 0
  References2D = -> [View]
  Rotation = 0
  Scale = 0.5
  ScaleType = 0
  TheoreticalExact = false
  Type = 5
  UnderTolerance = 0
  X = -23.0747
  Y = 6.9067
FEATURE [TechDraw::DrawViewDimension] Dimension011
  Arbitrary = false
  ArbitraryTolerances = false
  EqualTolerance = true
  FormatSpec = %.0f
  FormatSpecOverTolerance = %+.0f
  FormatSpecUnderTolerance = %+.0f
  Inverted = false
  LockPosition = false
  MeasureType = 1
  OverTolerance = 0
  References2D = -> [View]
  Rotation = 0
  Scale = 0.5
  ScaleType = 0
  TheoreticalExact = false
  Type = 1
  UnderTolerance = 0
  X = 22.9041
  Y = 46.3177
FEATURE [TechDraw::DrawViewDimension] Dimension012
  Arbitrary = false
  ArbitraryTolerances = false
  EqualTolerance = true
  FormatSpec = %.0f
  FormatSpecOverTolerance = %+.0f
  FormatSpecUnderTolerance = %+.0f
  Inverted = false
  LockPosition = false
  MeasureType = 1
  OverTolerance = 0
  References2D = -> [View]
  Rotation = 0
  Scale = 0.5
  ScaleType = 0
  TheoreticalExact = false
  Type = 1
  UnderTolerance = 0
  X = 26.2559
  Y = 28.0765
FEATURE [TechDraw::DrawViewDimension] Dimension013
  Arbitrary = false
  ArbitraryTolerances = false
  EqualTolerance = true
  FormatSpec = %.1f
  FormatSpecOverTolerance = %+.1f
  FormatSpecUnderTolerance = %+.1f
  Inverted = false
  LockPosition = false
  MeasureType = 1
  OverTolerance = 0
  References2D = -> [View]
  Rotation = 0
  Scale = 0.5
  ScaleType = 0
  TheoreticalExact = false
  Type = 2
  UnderTolerance = 0
  X = 45.81
  Y = -8.63325
FEATURE [TechDraw::DrawViewDimension] Dimension014
  Arbitrary = false
  ArbitraryTolerances = false
  EqualTolerance = true
  FormatSpec = ⌀%.1f
  FormatSpecOverTolerance = %+.1f
  FormatSpecUnderTolerance = %+.1f
  Inverted = false
  LockPosition = false
  MeasureType = 1
  OverTolerance = 0
  References2D = -> [View]
  Rotation = 0
  Scale = 0.5
  ScaleType = 0
  TheoreticalExact = false
  Type = 5
  UnderTolerance = 0
  X = 26.2468
  Y = -11.3901
FEATURE [TechDraw::DrawViewAnnotation] Annotation  label="   "
  Font = osifont
  LineSpace = 80
  LockPosition = false
  MaxWidth = -1
  Rotation = 0
  Scale = 0.5
  ScaleType = 0
  Text = M3 X 0.5 | 10mm DEEP
  TextSize = 5
  TextStyle = 0
  X = 166.576
  Y = 81.2293
FEATURE [TechDraw::DrawViewDimension] Dimension015
  Arbitrary = false
  ArbitraryTolerances = false
  EqualTolerance = true
  FormatSpec = %.1f
  FormatSpecOverTolerance = %+.1f
  FormatSpecUnderTolerance = %+.1f
  Inverted = false
  LockPosition = false
  MeasureType = 1
  OverTolerance = 0
  References2D = -> [View002]
  Rotation = 0
  Scale = 0.5
  ScaleType = 0
  TheoreticalExact = false
  Type = 2
  UnderTolerance = 0
  X = 23.5075
  Y = 23.7232
FEATURE [TechDraw::DrawViewDimension] Dimension016
  Arbitrary = false
  ArbitraryTolerances = false
  EqualTolerance = true
  FormatSpec = %.1f
  FormatSpecOverTolerance = %+.1f
  FormatSpecUnderTolerance = %+.1f
  Inverted = false
  LockPosition = false
  MeasureType = 1
  OverTolerance = 0
  References2D = -> [View002]
  Rotation = 0
  Scale = 0.5
  ScaleType = 0
  TheoreticalExact = false
  Type = 2
  UnderTolerance = 0
  X = 37.0052
  Y = 1.43385
FEATURE [TechDraw::DrawViewDimension] Dimension017
  Arbitrary = false
  ArbitraryTolerances = false
  EqualTolerance = true
  FormatSpec = %.1f
  FormatSpecOverTolerance = %+.1f
  FormatSpecUnderTolerance = %+.1f
  Inverted = false
  LockPosition = false
  MeasureType = 1
  OverTolerance = 0
  References2D = -> [View002]
  Rotation = 0
  Scale = 0.5
  ScaleType = 0
  TheoreticalExact = false
  Type = 2
  UnderTolerance = 0
  X = -23.5122
  Y = 22.3882
FEATURE [TechDraw::DrawViewDimension] Dimension018
  Arbitrary = false
  ArbitraryTolerances = false
  EqualTolerance = true
  FormatSpec = %.1f
  FormatSpecOverTolerance = %+.1f
  FormatSpecUnderTolerance = %+.1f
  Inverted = false
  LockPosition = false
  MeasureType = 1
  OverTolerance = 0
  References2D = -> [View002]
  Rotation = 0
  Scale = 0.5
  ScaleType = 0
  TheoreticalExact = false
  Type = 1
  UnderTolerance = 0
  X = -27.0831
  Y = 40.3806
FEATURE [TechDraw::DrawViewDimension] Dimension019
  Arbitrary = false
  ArbitraryTolerances = false
  EqualTolerance = true
  FormatSpec = %.1f
  FormatSpecOverTolerance = %+.1f
  FormatSpecUnderTolerance = %+.1f
  Inverted = false
  LockPosition = false
  MeasureType = 1
  OverTolerance = 0
  References2D = -> [View002]
  Rotation = 0
  Scale = 0.5
  ScaleType = 0
  TheoreticalExact = false
  Type = 1
  UnderTolerance = 0
  X = -39.7478
  Y = 45.9113
FEATURE [TechDraw::DrawViewDimension] Dimension020
  Arbitrary = false
  ArbitraryTolerances = false
  EqualTolerance = true
  FormatSpec = ⌀%.1f
  FormatSpecOverTolerance = %+.1f
  FormatSpecUnderTolerance = %+.1f
  Inverted = false
  LockPosition = false
  MeasureType = 1
  OverTolerance = 0
  References2D = -> [View002]
  Rotation = 0
  Scale = 0.5
  ScaleType = 0
  TheoreticalExact = false
  Type = 5
  UnderTolerance = 0
  X = -24.4347
  Y = 9.38597
FEATURE [TechDraw::DrawViewDimension] Dimension021
  Arbitrary = false
  ArbitraryTolerances = false
  EqualTolerance = true
  FormatSpec = ⌀%.1f
  FormatSpecOverTolerance = %+.1f
  FormatSpecUnderTolerance = %+.1f
  Inverted = false
  LockPosition = false
  MeasureType = 1
  OverTolerance = 0
  References2D = -> [View002]
  Rotation = 0
  Scale = 0.5
  ScaleType = 0
  TheoreticalExact = false
  Type = 5
  UnderTolerance = 0
  X = -20.6124
  Y = -5.37424
FEATURE [TechDraw::DrawViewDimension] Dimension022
  Arbitrary = false
  ArbitraryTolerances = false
  EqualTolerance = true
  FormatSpec = ⌀%.1f
  FormatSpecOverTolerance = %+.1f
  FormatSpecUnderTolerance = %+.1f
  Inverted = false
  LockPosition = false
  MeasureType = 1
  OverTolerance = 0
  References2D = -> [View002]
  Rotation = 0
  Scale = 0.5
  ScaleType = 0
  TheoreticalExact = false
  Type = 5
  UnderTolerance = 0
  X = 0.376729
  Y = 37.4845
FEATURE [TechDraw::DrawViewDimension] Dimension023
  Arbitrary = false
  ArbitraryTolerances = false
  EqualTolerance = true
  FormatSpec = ⌀%.1f
  FormatSpecOverTolerance = %+.1f
  FormatSpecUnderTolerance = %+.1f
  Inverted = false
  LockPosition = false
  MeasureType = 1
  OverTolerance = 0
  References2D = -> [View002]
  Rotation = 0
  Scale = 0.5
  ScaleType = 0
  TheoreticalExact = false
  Type = 5
  UnderTolerance = 0
  X = 12.0279
  Y = 21.0011
FEATURE [TechDraw::DrawViewDimension] Dimension024
  Arbitrary = false
  ArbitraryTolerances = false
  EqualTolerance = true
  FormatSpec = %.1f
  FormatSpecOverTolerance = %+.1f
  FormatSpecUnderTolerance = %+.1f
  Inverted = false
  LockPosition = false
  MeasureType = 1
  OverTolerance = 0
  References2D = -> [View002]
  Rotation = 0
  Scale = 0.5
  ScaleType = 0
  TheoreticalExact = false
  Type = 1
  UnderTolerance = 0
  X = -0.247613
  Y = -34.0422
FEATURE [TechDraw::DrawViewDimension] Dimension025
  Arbitrary = false
  ArbitraryTolerances = false
  EqualTolerance = true
  FormatSpec = %.1f
  FormatSpecOverTolerance = %+.1f
  FormatSpecUnderTolerance = %+.1f
  Inverted = false
  LockPosition = false
  MeasureType = 1
  OverTolerance = 0
  References2D = -> [View]
  Rotation = 0
  Scale = 0.5
  ScaleType = 0
  TheoreticalExact = false
  Type = 1
  UnderTolerance = 0
  X = 0.325494
  Y = -45.6472
FEATURE [TechDraw::DrawViewDimension] Dimension026
  Arbitrary = false
  ArbitraryTolerances = false
  EqualTolerance = true
  FormatSpec = %.1f
  FormatSpecOverTolerance = %+.1f
  FormatSpecUnderTolerance = %+.1f
  Inverted = false
  LockPosition = false
  MeasureType = 1
  OverTolerance = 0
  References2D = -> [View002]
  Rotation = 0
  Scale = 0.5
  ScaleType = 0
  TheoreticalExact = false
  Type = 2
  UnderTolerance = 0
  X = 27.6849
  Y = -15.5
FEATURE [TechDraw::DrawViewDimension] Dimension027
  Arbitrary = false
  ArbitraryTolerances = false
  EqualTolerance = true
  FormatSpec = %.1f
  FormatSpecOverTolerance = %+.1f
  FormatSpecUnderTolerance = %+.1f
  Inverted = false
  LockPosition = false
  MeasureType = 1
  OverTolerance = 0
  References2D = -> [View002]
  Rotation = 0
  Scale = 0.5
  ScaleType = 0
  TheoreticalExact = false
  Type = 2
  UnderTolerance = 0
  X = -27.951
  Y = -10.529
FEATURE [TechDraw::DrawPage] Page
  KeepUpdated = true
  NextBalloonIndex = 1
  ProjectionType = 1
  Scale = 0.5
  Template = -> Template
  Views = -> [View,Dimension,Dimension002,Dimension003,View001,View002,Dimension004,Dimension005,Dimension006,Dimension007,Dimension008,Dimension010,Dimension011,Dimension012,Dimension013,Dimension014,Annotation,Dimension015,Dimension016,Dimension017,Dimension018,Dimension019,Dimension020,Dimension021,Dimension022,Dimension023,Dimension024,Dimension025,Dimension026,Dimension027]
---- part bearing_linear_8mm_horiz.FCStd = doc fcstd_05b5c3e2a6bc ----
FCSTD DOCUMENT  (FreeCAD 0.19R)
Label: bearing_linear_8mm_horiz
License: All rights reserved
LicenseURL: http://en.wikipedia.org/wiki/All_rights_reserved
objects: PartDesign::CoordinateSystem×5, Sketcher::SketchObject×2, PartDesign::Pad×1, PartDesign::Pocket×1, PartDesign::Hole×1, PartDesign::Body×1
note: 14 computed .brp shape members not serialized (recipe doc carries the construction recipe); baked Part::Feature solids carry a one-line shape summary decoded from their .brp

FEATURE [Sketcher::SketchObject] Sketch
  FullyConstrained = false
  MapMode = 5
  Placement = pos=(0,0,0) rot=(1,0,0;1.5708rad)
  Support = -> [XZ_Plane]
  sketch-geometry (18):
    g0: LineSegment StartX=16 StartY=7 StartZ=0 EndX=16 EndY=-3 EndZ=0
    g1: LineSegment StartX=16 StartY=-3 StartZ=0 EndX=17 EndY=-5 EndZ=0
    g2: LineSegment StartX=17 StartY=-5 StartZ=0 EndX=17 EndY=-11 EndZ=0
    g3: LineSegment StartX=17 StartY=-11 StartZ=0 EndX=7 EndY=-11 EndZ=0
    g4: LineSegment StartX=7 StartY=-11 StartZ=0 EndX=6 EndY=-9 EndZ=0
    g5: LineSegment StartX=16 StartY=7 StartZ=0 EndX=7.5 EndY=7 EndZ=0
    g6: LineSegment StartX=7.5 StartY=7 StartZ=0 EndX=3.5 EndY=11 EndZ=0
    g7: Circle CenterX=0 CenterY=0 CenterZ=0 NormalX=0 NormalY=0 NormalZ=1 AngleXU=0 Radius=4
    g8: LineSegment StartX=0 StartY=0 StartZ=0 EndX=0 EndY=36.8082 EndZ=0
    g9: LineSegment StartX=-3.5 StartY=11 StartZ=0 EndX=-7.5 EndY=7 EndZ=0
    g10: LineSegment StartX=-7.5 StartY=7 StartZ=0 EndX=-16 EndY=7 EndZ=0
    g11: LineSegment StartX=-16 StartY=7 StartZ=0 EndX=-16 EndY=-3 EndZ=0
    g12: LineSegment StartX=-16 StartY=-3 StartZ=0 EndX=-17 EndY=-5 EndZ=0
    g13: LineSegment StartX=-17 StartY=-5 StartZ=0 EndX=-17 EndY=-11 EndZ=0
    g14: LineSegment StartX=-17 StartY=-11 StartZ=0 EndX=-7 EndY=-11 EndZ=0
    g15: LineSegment StartX=-7 StartY=-11 StartZ=0 EndX=-6 EndY=-9 EndZ=0
    g16: LineSegment StartX=-6 StartY=-9 StartZ=0 EndX=6 EndY=-9 EndZ=0
    g17: LineSegment StartX=3.5 StartY=11 StartZ=0 EndX=-3.5 EndY=11 EndZ=0
  constraints (45):
    c: Vertical(g0)
    c: Coincident(g1,g0)
    c: Coincident(g2,g1)
    c: Vertical(g2)
    c: Coincident(g2,g3)
    c: Horizontal(g3)
    c: Coincident(g3,g4)
    c: Coincident(g0,g5)
    c: Horizontal(g5)
    c: Coincident(g5,g6)
    c: Coincident(g7,g-1)
    c: Diameter(g7) = 8
    c: DistanceY(g2,g6) = 22
    c: DistanceY(g2,g0) = 18
    c: Coincident(g8,g7)
    c: PointOnObject(g8,g-2)
    c: Coincident(g9,g10)
    c: Coincident(g10,g11)
    c: Coincident(g11,g12)
    c: Coincident(g12,g13)
    c: Vertical(g13)
    c: Coincident(g13,g14)
    c: Horizontal(g14)
    c: Coincident(g14,g15)
    c: Coincident(g15,g16)
    c: Coincident(g16,g4)
    c: Coincident(g6,g17)
    c: Coincident(g17,g9)
    c: Symmetric(g9,g6,g8)
    c: Symmetric(g4,g15,g8)
    c: Symmetric(g9,g5,g8)
    c: Symmetric(g10,g0,g8)
    c: Symmetric(g1,g12,g8)
    c: Symmetric(g0,g11,g8)
    c: Symmetric(g14,g3,g8)
    c: DistanceY(g2,g7) = 11
    c: DistanceX(g12,g1) = 34
    c: DistanceY(g3,g4) = 2
    c: DistanceX(g16,g16) = 12
    c: DistanceX(g14,g3) = 14
    c: DistanceY(g2,g2) = 6
    c: DistanceY(g2,g0) = 8
    c: DistanceX(g0,g1) = 1
    c: DistanceX(g9,g5) = 15
    c: Angle(g17,g6) = 2.35619
FEATURE [PartDesign::Pad] Pad
  Direction = (1,1,1)
  Length = 30
  Length2 = 100
  Midplane = true
  Placement = pos=(0,0,0) rot=(1,0,0;1.5708rad)
  Profile = -> Sketch
  Refine = true
  Type = 0
FEATURE [Sketcher::SketchObject] Sketch001
  FullyConstrained = true
  MapMode = 5
  Support = -> [XY_Plane]
  sketch-geometry (4):
    g0: Circle CenterX=-12 CenterY=9 CenterZ=0 NormalX=0 NormalY=0 NormalZ=1 AngleXU=0 Radius=1.75
    g1: Circle CenterX=12 CenterY=9 CenterZ=0 NormalX=0 NormalY=0 NormalZ=1 AngleXU=0 Radius=1.75
    g2: Circle CenterX=12 CenterY=-9 CenterZ=0 NormalX=0 NormalY=0 NormalZ=1 AngleXU=0 Radius=1.75
    g3: Circle CenterX=-12 CenterY=-9 CenterZ=0 NormalX=0 NormalY=0 NormalZ=1 AngleXU=0 Radius=1.75
  constraints (10):
    c: Equal(g1,g2)
    c: Equal(g2,g0)
    c: Equal(g0,g3)
    c: Symmetric(g0,g2,g-1)
    c: Symmetric(g1,g3,g-1)
    c: Vertical(g1,g2)
    c: Horizontal(g1,g0)
    c: DistanceX(g3,g2) = 24
    c: DistanceY(g2,g1) = 18
    c: Diameter(g1) = 3.5
FEATURE [PartDesign::Pocket] Pocket
  BaseFeature = -> Pad
  Length = 5
  Length2 = 100
  Midplane = true
  Placement = pos=(0,0,0) rot=(1,0,0;1.5708rad)
  Profile = -> Sketch001
  Refine = true
  Type = 1
FEATURE [PartDesign::Hole] Hole
  BaseFeature = -> Pocket
  Depth = 25
  DepthType = 0
  Diameter = 3.3
  DrillForDepth = false
  DrillPoint = 1
  DrillPointAngle = 118
  HoleCutCountersinkAngle = 90
  HoleCutCustomValues = false
  HoleCutDepth = 0
  HoleCutDiameter = 6.1
  HoleCutType = 2
  ModelActualThread = false
  Placement = pos=(0,0,0) rot=(1,0,0;1.5708rad)
  Profile = -> Sketch001
  Refine = true
  Tapered = false
  TaperedAngle = 90
  ThreadAngle = 60
  ThreadClass = 0
  ThreadCutOffInner = 0.0757772
  ThreadCutOffOuter = 0.151554
  ThreadDirection = 0
  ThreadFit = 0
  ThreadPitch = 0.7
  ThreadSize = 11
  ThreadType = 1
  Threaded = true
FEATURE [PartDesign::CoordinateSystem] Local_CS
  AttacherType = Attacher::AttachEngine3D
  MapMode = 11
  Placement = pos=(-12,-9,-11) rot=(0,0,1;1.5708rad)
  Support = -> [Hole]
FEATURE [PartDesign::CoordinateSystem] Local_CS001
  AttacherType = Attacher::AttachEngine3D
  MapMode = 11
  Placement = pos=(12,9,-11) rot=(0,0,1;1.5708rad)
  Support = -> [Hole]
FEATURE [PartDesign::CoordinateSystem] Local_CS002
  AttacherType = Attacher::AttachEngine3D
FEATURE [PartDesign::CoordinateSystem] Local_CS003
  AttacherType = Attacher::AttachEngine3D
  MapMode = 11
  Placement = pos=(12,-9,-11) rot=(0,0,1;1.5708rad)
  Support = -> [Hole]
FEATURE [PartDesign::CoordinateSystem] Local_CS004
  AttacherType = Attacher::AttachEngine3D
  MapMode = 11
  Placement = pos=(-12,9,-11) rot=(0,0,1;1.5708rad)
  Support = -> [Hole]
FEATURE [PartDesign::Body] Body
  Group = -> [Sketch,Pad,Sketch001,Pocket,Hole,Local_CS,Local_CS001,Local_CS002,Local_CS003,Local_CS004]
  Origin = -> Origin
  Tip = -> Hole
---- part bracket_nema_17.FCStd = doc fcstd_1117811c538f ----
FCSTD DOCUMENT  (FreeCAD 0.19R)
Label: bracket_nema_17
License: All rights reserved
LicenseURL: http://en.wikipedia.org/wiki/All_rights_reserved
objects: PartDesign::CoordinateSystem×6, Sketcher::SketchObject×5, PartDesign::Pad×3, PartDesign::Pocket×3, PartDesign::Chamfer×2, PartDesign::Mirrored×1, PartDesign::Body×1
note: 29 computed .brp shape members not serialized (recipe doc carries the construction recipe); baked Part::Feature solids carry a one-line shape summary decoded from their .brp

FEATURE [Sketcher::SketchObject] Sketch
  FullyConstrained = true
  MapMode = 5
  Support = -> [XY_Plane]
  sketch-geometry (4):
    g0: LineSegment StartX=-25 StartY=25.5 StartZ=0 EndX=25 EndY=25.5 EndZ=0
    g1: LineSegment StartX=25 StartY=25.5 StartZ=0 EndX=25 EndY=-25.5 EndZ=0
    g2: LineSegment StartX=25 StartY=-25.5 StartZ=0 EndX=-25 EndY=-25.5 EndZ=0
    g3: LineSegment StartX=-25 StartY=-25.5 StartZ=0 EndX=-25 EndY=25.5 EndZ=0
  constraints (10):
    c: Coincident(g0,g1)
    c: Coincident(g1,g2)
    c: Coincident(g2,g3)
    c: Coincident(g3,g0)
    c: Symmetric(g0,g1,g-1)
    c: Symmetric(g0,g2,g-1)
    c: Vertical(g0,g1)
    c: Horizontal(g0,g0)
    c: DistanceX(g2,g2) = 50
    c: DistanceY(g1,g1) = 51
FEATURE [PartDesign::Pad] Pad
  Direction = (1,1,1)
  Length = 3
  Length2 = 100
  Profile = -> Sketch
  Refine = true
  Type = 0
FEATURE [PartDesign::Chamfer] Chamfer
  Angle = 45
  Base = -> Pad [Edge5,Edge8]
  BaseFeature = -> Pad
  ChamferType = 0
  FlipDirection = false
  Refine = true
  Size = 5
  Size2 = 1
  SupportTransform = false
FEATURE [Sketcher::SketchObject] Sketch001
  ExternalGeometry = -> [Chamfer]
  FullyConstrained = true
  MapMode = 5
  Placement = pos=(0,25.5,0) rot=(0,0.707107,0.707107;3.14159rad)
  Support = -> [Chamfer]
  sketch-geometry (4):
    g0: LineSegment StartX=-25 StartY=0 StartZ=0 EndX=-25 EndY=51 EndZ=0
    g1: LineSegment StartX=-25 StartY=51 StartZ=0 EndX=25 EndY=51 EndZ=0
    g2: LineSegment StartX=25 StartY=51 StartZ=0 EndX=25 EndY=0 EndZ=0
    g3: LineSegment StartX=-25 StartY=0 StartZ=0 EndX=25 EndY=0 EndZ=0
  constraints (10):
    c: Coincident(g-3,g0)
    c: Vertical(g0)
    c: Coincident(g0,g1)
    c: Horizontal(g1)
    c: Coincident(g1,g2)
    c: Coincident(g2,g-3)
    c: Vertical(g2)
    c: DistanceY(g2,g2) = 51
    c: Coincident(g0,g3)
    c: Coincident(g3,g2)
FEATURE [PartDesign::Pad] Pad001
  BaseFeature = -> Chamfer
  Direction = (1,1,1)
  Length = 3
  Length2 = 100
  Profile = -> Sketch001
  Refine = true
  Type = 0
FEATURE [PartDesign::Chamfer] Chamfer001
  Angle = 45
  Base = -> Pad001 [Edge18,Edge17]
  BaseFeature = -> Pad001
  ChamferType = 0
  FlipDirection = false
  Refine = true
  Size = 5
  Size2 = 1
  SupportTransform = false
FEATURE [Sketcher::SketchObject] Sketch002
  ExternalGeometry = -> [Chamfer001]
  FullyConstrained = true
  MapMode = 5
  Placement = pos=(0,0,0) rot=(1,0,0;1.5708rad)
  Support = -> [XZ_Plane]
  sketch-geometry (4):
    g0: ArcOfCircle CenterX=-15.015 CenterY=39.85 CenterZ=0 NormalX=0 NormalY=0 NormalZ=1 AngleXU=0 Radius=2.15 StartAngle=-1.07e-14 EndAngle=3.14159
    g1: ArcOfCircle CenterX=-15.015 CenterY=10.15 CenterZ=0 NormalX=0 NormalY=0 NormalZ=1 AngleXU=0 Radius=2.15 StartAngle=3.14159 EndAngle=6.28319
    g2: LineSegment StartX=-17.165 StartY=39.85 StartZ=0 EndX=-17.165 EndY=10.15 EndZ=0
    g3: LineSegment StartX=-12.865 StartY=39.85 StartZ=0 EndX=-12.865 EndY=10.15 EndZ=0
  constraints (10):
    c: Tangent(g0,g3) = 1.5708
    c: Tangent(g0,g2) = -1.5708
    c: Tangent(g2,g1) = -1.5708
    c: Tangent(g3,g1) = 1.5708
    c: Vertical(g2)
    c: Equal(g0,g1)
    c: DistanceX(g0,g0) = 4.3
    c: DistanceY(g1,g0) = 29.7
    c: DistanceX(g1,g-1) = 12.865
    c: DistanceY(g0,g-3) = 11.15
FEATURE [PartDesign::Pocket] Pocket
  BaseFeature = -> Chamfer001
  Length = 5
  Length2 = 100
  Profile = -> Sketch002
  Refine = true
  Type = 1
FEATURE [PartDesign::Mirrored] Mirrored
  BaseFeature = -> Pocket
  MirrorPlane = -> Sketch002 [V_Axis]
  Originals = -> [Pocket]
  Refine = true
FEATURE [Sketcher::SketchObject] Sketch003
  ExternalGeometry = -> [Mirrored]
  FullyConstrained = true
  MapMode = 5
  Support = -> [XY_Plane]
  sketch-geometry (10):
    g0: LineSegment StartX=15.5 StartY=11 StartZ=0 EndX=-15.5 EndY=11 EndZ=0
    g1: LineSegment StartX=-15.5 StartY=11 StartZ=0 EndX=-15.5 EndY=-20 EndZ=0
    g2: LineSegment StartX=-15.5 StartY=-20 StartZ=0 EndX=15.5 EndY=-20 EndZ=0
    g3: LineSegment StartX=15.5 StartY=-20 StartZ=0 EndX=15.5 EndY=11 EndZ=0
    g4: Circle CenterX=0 CenterY=-4.5 CenterZ=0 NormalX=0 NormalY=0 NormalZ=1 AngleXU=0 Radius=21.9203
    g5: Circle CenterX=-15.5 CenterY=11 CenterZ=0 NormalX=0 NormalY=0 NormalZ=1 AngleXU=0 Radius=1.5
    g6: Circle CenterX=15.5 CenterY=11 CenterZ=0 NormalX=0 NormalY=0 NormalZ=1 AngleXU=0 Radius=1.5
    g7: Circle CenterX=15.5 CenterY=-20 CenterZ=0 NormalX=0 NormalY=0 NormalZ=1 AngleXU=0 Radius=1.5
    g8: Circle CenterX=-15.5 CenterY=-20 CenterZ=0 NormalX=0 NormalY=0 NormalZ=1 AngleXU=0 Radius=1.5
    g9: Circle CenterX=0 CenterY=-4.5 CenterZ=0 NormalX=0 NormalY=0 NormalZ=1 AngleXU=0 Radius=11
  constraints (24):
    c: Coincident(g0,g1)
    c: Coincident(g1,g2)
    c: Coincident(g2,g3)
    c: Coincident(g3,g0)
    c: Equal(g0,g1)
    c: Equal(g0,g2)
    c: Equal(g0,g3)
    c: PointOnObject(g0,g4)
    c: PointOnObject(g1,g4)
    c: PointOnObject(g2,g4)
    c: PointOnObject(g3,g4)
    c: DistanceX(g2,g2) = 31
    c: Coincident(g5,g0)
    c: Coincident(g6,g0)
    c: Coincident(g7,g2)
    c: Coincident(g8,g1)
    c: Equal(g5,g7)
    c: Equal(g7,g6)
    c: Equal(g6,g8)
    c: Diameter(g6) = 3
    c: Symmetric(g7,g8,g-2)
    c: DistanceY(g-3,g4) = 21
    c: Coincident(g9,g4)
    c: Diameter(g9) = 22
FEATURE [PartDesign::Pocket] Pocket001
  BaseFeature = -> Mirrored
  Length = 5
  Length2 = 100
  Midplane = true
  Profile = -> Sketch003
  Refine = true
  Type = 1
FEATURE [Sketcher::SketchObject] Sketch004
  ExternalGeometry = -> [Pocket001]
  FullyConstrained = true
  MapMode = 5
  Placement = pos=(0,0,0) rot=(0.57735,0.57735,0.57735;2.0944rad)
  Support = -> [YZ_Plane]
  sketch-geometry (3):
    g0: LineSegment StartX=25.5 StartY=22 StartZ=0 EndX=6.5 EndY=3 EndZ=0
    g1: LineSegment StartX=6.5 StartY=3 StartZ=0 EndX=25.5 EndY=3 EndZ=0
    g2: LineSegment StartX=25.5 StartY=22 StartZ=0 EndX=25.5 EndY=3 EndZ=0
  constraints (8):
    c: PointOnObject(g0,g-3)
    c: PointOnObject(g0,g-4)
    c: Coincident(g1,g0)
    c: Coincident(g1,g-4)
    c: Coincident(g2,g0)
    c: Coincident(g2,g1)
    c: Equal(g2,g1)
    c: DistanceX(g1,g1) = 19
FEATURE [PartDesign::Pad] Pad002
  BaseFeature = -> Pocket001
  Direction = (1,1,1)
  Length = 50
  Length2 = 100
  Midplane = true
  Offset = -3
  Profile = -> Sketch004
  Refine = true
  Type = 0
FEATURE [PartDesign::Pocket] Pocket002
  BaseFeature = -> Pad002
  Length = 44
  Length2 = 100
  Midplane = true
  Profile = -> Sketch004
  Refine = true
  Type = 0
FEATURE [PartDesign::CoordinateSystem] Local_CS
  AttacherType = Attacher::AttachEngine3D
  MapMode = 11
  Placement = pos=(0,-4.5,3) rot=(0,0,1;3.14159rad)
  Support = -> [Pocket002]
FEATURE [PartDesign::CoordinateSystem] Local_CS001
  AttacherType = Attacher::AttachEngine3D
  MapMode = 11
  Placement = pos=(0,-4.5,0) rot=(0,0,1;1.5708rad)
  Support = -> [Pocket002]
FEATURE [PartDesign::CoordinateSystem] Local_CS002
  AttacherType = Attacher::AttachEngine3D
  MapMode = 11
  Placement = pos=(15.015,28.5,10.15) rot=(0.57735,0.57735,-0.57735;2.0944rad)
  Support = -> [Pocket002]
FEATURE [PartDesign::CoordinateSystem] Local_CS003
  AttacherType = Attacher::AttachEngine3D
  MapMode = 11
  Placement = pos=(-15.015,28.5,39.85) rot=(0.57735,-0.57735,0.57735;2.0944rad)
  Support = -> [Pocket002]
FEATURE [PartDesign::CoordinateSystem] Local_CS004
  AttacherType = Attacher::AttachEngine3D
  MapMode = 11
  Placement = pos=(15.015,28.5,39.85) rot=(0.57735,-0.57735,0.57735;2.0944rad)
  Support = -> [Pocket002]
FEATURE [PartDesign::CoordinateSystem] Local_CS005
  AttacherType = Attacher::AttachEngine3D
  MapMode = 11
  Placement = pos=(-15.015,28.5,10.15) rot=(0.57735,0.57735,-0.57735;2.0944rad)
  Support = -> [Pocket002]
FEATURE [PartDesign::Body] Body
  Group = -> [Sketch,Pad,Chamfer,Sketch001,Pad001,Chamfer001,Sketch002,Pocket,Mirrored,Sketch003,Pocket001,Sketch004,Pad002,Pocket002,Local_CS,Local_CS001,Local_CS002,Local_CS003,Local_CS004,Local_CS005]
  Origin = -> Origin
  Tip = -> Pocket002
---- part coupling_8mm_5mm.FCStd = doc fcstd_2b3f350c5686 ----
FCSTD DOCUMENT  (FreeCAD 0.19R)
Label: coupling_8mm_5mm
License: All rights reserved
LicenseURL: http://en.wikipedia.org/wiki/All_rights_reserved
objects: Sketcher::SketchObject×3, PartDesign::Pocket×2, PartDesign::CoordinateSystem×2, PartDesign::Pad×1, PartDesign::Body×1
note: 12 computed .brp shape members not serialized (recipe doc carries the construction recipe); baked Part::Feature solids carry a one-line shape summary decoded from their .brp

FEATURE [Sketcher::SketchObject] Sketch
  FullyConstrained = true
  MapMode = 5
  Support = -> [XY_Plane]
  sketch-geometry (1):
    g0: Circle CenterX=0 CenterY=0 CenterZ=0 NormalX=0 NormalY=0 NormalZ=1 AngleXU=0 Radius=9.5
  constraints (2):
    c: Coincident(g0,g-1)
    c: Diameter(g0) = 19
FEATURE [PartDesign::Pad] Pad
  Direction = (1,1,1)
  Length = 25
  Length2 = 100
  Midplane = true
  Profile = -> Sketch
  Refine = true
  Type = 0
FEATURE [Sketcher::SketchObject] Sketch001
  FullyConstrained = true
  MapMode = 5
  Support = -> [XY_Plane]
  sketch-geometry (1):
    g0: Circle CenterX=0 CenterY=0 CenterZ=0 NormalX=0 NormalY=0 NormalZ=1 AngleXU=0 Radius=2.5
  constraints (2):
    c: Coincident(g0,g-1)
    c: Diameter(g0) = 5
FEATURE [PartDesign::Pocket] Pocket
  BaseFeature = -> Pad
  Length = 5
  Length2 = 100
  Midplane = true
  Profile = -> Sketch001
  Refine = true
  Type = 1
FEATURE [Sketcher::SketchObject] Sketch002
  FullyConstrained = true
  MapMode = 5
  Support = -> [XY_Plane]
  sketch-geometry (1):
    g0: Circle CenterX=0 CenterY=0 CenterZ=0 NormalX=0 NormalY=0 NormalZ=1 AngleXU=0 Radius=4
  constraints (2):
    c: Coincident(g0,g-1)
    c: Diameter(g0) = 8
FEATURE [PartDesign::Pocket] Pocket001
  BaseFeature = -> Pocket
  Length = 5
  Length2 = 100
  Profile = -> Sketch002
  Refine = true
  Type = 1
FEATURE [PartDesign::CoordinateSystem] Local_CS
  AttacherType = Attacher::AttachEngine3D
  MapMode = 11
  Placement = pos=(0,0,12.5) rot=(0,0,1;1.5708rad)
  Support = -> [Pocket001]
FEATURE [PartDesign::CoordinateSystem] Local_CS001
  AttacherType = Attacher::AttachEngine3D
  MapMode = 11
  Placement = pos=(0,0,-12.5) rot=(0,0,1;1.5708rad)
  Support = -> [Pocket001]
FEATURE [PartDesign::Body] Body
  Group = -> [Sketch,Pad,Sketch001,Pocket,Sketch002,Pocket001,Local_CS,Local_CS001]
  Origin = -> Origin
  Tip = -> Pocket001
---- part nut_angle.FCStd = doc fcstd_4160f186e784 ----
FCSTD DOCUMENT  (FreeCAD 0.19R)
Label: nut_angle
License: All rights reserved
LicenseURL: http://en.wikipedia.org/wiki/All_rights_reserved
objects: Sketcher::SketchObject×3, PartDesign::CoordinateSystem×3, PartDesign::Pad×1, PartDesign::Pocket×1, PartDesign::Hole×1, PartDesign::Body×1
note: 13 computed .brp shape members not serialized (recipe doc carries the construction recipe); baked Part::Feature solids carry a one-line shape summary decoded from their .brp

FEATURE [Sketcher::SketchObject] Sketch
  FullyConstrained = true
  MapMode = 5
  Placement = pos=(0,0,0) rot=(0.57735,0.57735,0.57735;2.0944rad)
  Support = -> [YZ_Plane]
  sketch-geometry (6):
    g0: LineSegment StartX=-28 StartY=0 StartZ=0 EndX=0 EndY=0 EndZ=0
    g1: LineSegment StartX=0 StartY=0 StartZ=0 EndX=0 EndY=-34 EndZ=0
    g2: LineSegment StartX=0 StartY=-34 StartZ=0 EndX=-6.35 EndY=-34 EndZ=0
    g3: LineSegment StartX=-6.35 StartY=-34 StartZ=0 EndX=-6.35 EndY=-6.35 EndZ=0
    g4: LineSegment StartX=-6.35 StartY=-6.35 StartZ=0 EndX=-28 EndY=-6.35 EndZ=0
    g5: LineSegment StartX=-28 StartY=-6.35 StartZ=0 EndX=-28 EndY=0 EndZ=0
  constraints (17):
    c: PointOnObject(g0,g-1)
    c: Coincident(g0,g1)
    c: PointOnObject(g1,g-2)
    c: Coincident(g1,g2)
    c: Horizontal(g2)
    c: Coincident(g2,g3)
    c: Vertical(g3)
    c: Coincident(g3,g4)
    c: Horizontal(g4)
    c: Coincident(g4,g5)
    c: Coincident(g5,g0)
    c: Vertical(g5)
    c: Coincident(g-1,g0)
    c: Equal(g2,g5)
    c: DistanceX(g0,g0) = 28
    c: DistanceX(g2,g2) = 6.35
    c: DistanceY(g1,g1) = 34
FEATURE [PartDesign::Pad] Pad
  Direction = (1,1,1)
  Length = 22
  Length2 = 100
  Midplane = true
  Placement = pos=(0,0,0) rot=(0.57735,0.57735,0.57735;2.0944rad)
  Profile = -> Sketch
  Refine = true
  Type = 0
FEATURE [Sketcher::SketchObject] Sketch002
  FullyConstrained = true
  MapMode = 5
  Support = -> [XY_Plane]
  sketch-geometry (7):
    g0: Circle CenterX=0 CenterY=-16.5 CenterZ=0 NormalX=0 NormalY=0 NormalZ=1 AngleXU=0 Radius=5
    g1: Circle CenterX=-5.65685 CenterY=-22.1569 CenterZ=0 NormalX=0 NormalY=0 NormalZ=1 AngleXU=0 Radius=1.75
    g2: Circle CenterX=5.65685 CenterY=-22.1569 CenterZ=0 NormalX=0 NormalY=0 NormalZ=1 AngleXU=0 Radius=1.75
    g3: Circle CenterX=5.65685 CenterY=-10.8431 CenterZ=0 NormalX=0 NormalY=0 NormalZ=1 AngleXU=0 Radius=1.75
    g4: Circle CenterX=-5.65685 CenterY=-10.8431 CenterZ=0 NormalX=0 NormalY=0 NormalZ=1 AngleXU=0 Radius=1.75
    g5: LineSegment StartX=-5.65685 StartY=-10.8431 StartZ=0 EndX=5.65685 EndY=-10.8431 EndZ=0
    g6: LineSegment StartX=-5.65685 StartY=-10.8431 StartZ=0 EndX=-5.65685 EndY=-22.1569 EndZ=0
  constraints (17):
    c: PointOnObject(g0,g-2)
    c: Diameter(g0) = 10
    c: DistanceY(g0,g-1) = 16.5
    c: Horizontal(g4,g3)
    c: Symmetric(g4,g2,g0)
    c: Symmetric(g1,g3,g0)
    c: Vertical(g3,g2)
    c: Equal(g4,g3)
    c: Equal(g2,g1)
    c: Equal(g1,g3)
    c: Diameter(g2) = 3.5
    c: Coincident(g5,g4)
    c: Coincident(g5,g3)
    c: Coincident(g6,g4)
    c: Coincident(g6,g1)
    c: Equal(g6,g5)
    c: Distance(g3,g1) = 16
FEATURE [PartDesign::Pocket] Pocket
  BaseFeature = -> Pad
  Length = 5
  Length2 = 100
  Midplane = true
  Placement = pos=(0,0,0) rot=(0.57735,0.57735,0.57735;2.0944rad)
  Profile = -> Sketch002
  Refine = true
  Type = 1
FEATURE [Sketcher::SketchObject] Sketch003
  FullyConstrained = true
  MapMode = 5
  Placement = pos=(0,0,0) rot=(0.57735,0.57735,0.57735;4.18879rad)
  Support = -> [Pocket]
  sketch-geometry (5):
    g0: Circle CenterX=-27.5 CenterY=7.5 CenterZ=0 NormalX=0 NormalY=0 NormalZ=1 AngleXU=0 Radius=1
    g1: Circle CenterX=-12.5 CenterY=7.5 CenterZ=0 NormalX=0 NormalY=0 NormalZ=1 AngleXU=0 Radius=1
    g2: Circle CenterX=-12.5 CenterY=-7.5 CenterZ=0 NormalX=0 NormalY=0 NormalZ=1 AngleXU=0 Radius=1
    g3: Circle CenterX=-27.5 CenterY=-7.5 CenterZ=0 NormalX=0 NormalY=0 NormalZ=1 AngleXU=0 Radius=1
    g4: GeomPoint X=-20 Y=0 Z=0
  constraints (11):
    c: Symmetric(g0,g3,g-1)
    c: Symmetric(g1,g2,g-1)
    c: PointOnObject(g4,g-1)
    c: Symmetric(g1,g3,g4)
    c: Equal(g0,g1)
    c: Equal(g1,g2)
    c: Equal(g2,g3)
    c: Diameter(g1) = 2
    c: DistanceX(g0,g1) = 15
    c: DistanceY(g3,g0) = 15
    c: DistanceX(g4,g-1) = 20
FEATURE [PartDesign::Hole] Hole
  BaseFeature = -> Pocket
  Depth = 25
  DepthType = 1
  Diameter = 3.2
  DrillForDepth = false
  DrillPoint = 1
  DrillPointAngle = 118
  HoleCutCountersinkAngle = 90
  HoleCutCustomValues = false
  HoleCutDepth = 0
  HoleCutDiameter = 6.1
  HoleCutType = 0
  ModelActualThread = false
  Placement = pos=(0,0,0) rot=(0.57735,0.57735,0.57735;2.0944rad)
  Profile = -> Sketch003
  Refine = true
  Tapered = false
  TaperedAngle = 90
  ThreadAngle = 0
  ThreadClass = 0
  ThreadCutOffInner = 0
  ThreadCutOffOuter = 0
  ThreadDirection = 0
  ThreadFit = 1
  ThreadPitch = 0
  ThreadSize = 9
  ThreadType = 1
  Threaded = false
FEATURE [PartDesign::CoordinateSystem] Local_CS
  AttacherType = Attacher::AttachEngine3D
  MapMode = 11
  Placement = pos=(7.5,-1.1e-14,-27.5) rot=(0.57735,0.57735,0.57735;4.18879rad)
  Support = -> [Hole]
FEATURE [PartDesign::CoordinateSystem] Local_CS001
  AttacherType = Attacher::AttachEngine3D
  MapMode = 11
  Placement = pos=(3.6e-15,-16.5,0) rot=(0,0,1;1.5708rad)
  Support = -> [Hole]
FEATURE [PartDesign::CoordinateSystem] Local_CS002
  AttacherType = Attacher::AttachEngine3D
  MapMode = 11
  Placement = pos=(5.65685,-22.1569,7.1e-15) rot=(0,0,1;1.5708rad)
  Support = -> [Hole]
FEATURE [PartDesign::Body] Body
  Group = -> [Sketch,Pad,Sketch002,Pocket,Sketch003,Hole,Local_CS,Local_CS001,Local_CS002]
  Origin = -> Origin
  Tip = -> Hole
---- part nut_lead_screw_tr8x4.FCStd = doc fcstd_da8f933943eb ----
FCSTD DOCUMENT  (FreeCAD 0.19R)
Label: nut_lead_screw_tr8x4
License: All rights reserved
LicenseURL: http://en.wikipedia.org/wiki/All_rights_reserved
objects: Sketcher::SketchObject×3, PartDesign::CoordinateSystem×3, PartDesign::Revolution×1, PartDesign::Pocket×1, PartDesign::Hole×1, PartDesign::PolarPattern×1, PartDesign::Body×1
note: 14 computed .brp shape members not serialized (recipe doc carries the construction recipe); baked Part::Feature solids carry a one-line shape summary decoded from their .brp

FEATURE [Sketcher::SketchObject] Sketch
  FullyConstrained = true
  MapMode = 5
  Placement = pos=(0,0,0) rot=(0.57735,0.57735,0.57735;2.0944rad)
  Support = -> [YZ_Plane]
  sketch-geometry (8):
    g0: LineSegment StartX=0 StartY=0 StartZ=0 EndX=11 EndY=0 EndZ=0
    g1: LineSegment StartX=11 StartY=0 StartZ=0 EndX=11 EndY=-4 EndZ=0
    g2: LineSegment StartX=11 StartY=-4 StartZ=0 EndX=5.15 EndY=-4 EndZ=0
    g3: LineSegment StartX=5.15 StartY=-4 StartZ=0 EndX=5.15 EndY=-22 EndZ=0
    g4: LineSegment StartX=7 StartY=-26 StartZ=0 EndX=0 EndY=-26 EndZ=0
    g5: LineSegment StartX=0 StartY=-26 StartZ=0 EndX=0 EndY=0 EndZ=0
    g6: LineSegment StartX=5.15 StartY=-22 StartZ=0 EndX=7 EndY=-22 EndZ=0
    g7: LineSegment StartX=7 StartY=-22 StartZ=0 EndX=7 EndY=-26 EndZ=0
  constraints (23):
    c: Horizontal(g0)
    c: Vertical(g1)
    c: Coincident(g1,g2)
    c: Horizontal(g2)
    c: Coincident(g2,g3)
    c: Vertical(g3)
    c: PointOnObject(g4,g-2)
    c: Horizontal(g4)
    c: Coincident(g4,g5)
    c: Coincident(g5,g0)
    c: Horizontal(g6)
    c: Coincident(g7,g6)
    c: Vertical(g7)
    c: Coincident(g3,g6)
    c: Coincident(g4,g7)
    c: DistanceX(g-1,g4) = 7
    c: Coincident(g1,g0)
    c: Coincident(g-1,g0)
    c: DistanceX(g0,g0) = 11
    c: DistanceX(g0,g2) = 5.15
    c: DistanceY(g1,g1) = 4
    c: DistanceY(g5,g5) = 26
    c: DistanceY(g7,g7) = 4
FEATURE [PartDesign::Revolution] Revolution
  Angle = 360
  Axis = (-2e-16,3e-16,1)
  Base = (0,0,0)
  Placement = pos=(0,0,0) rot=(0.57735,0.57735,0.57735;2.0944rad)
  Profile = -> Sketch
  ReferenceAxis = -> Sketch [V_Axis]
  Reversed = true
FEATURE [Sketcher::SketchObject] Sketch001
  FullyConstrained = true
  MapMode = 5
  Support = -> [XY_Plane]
  sketch-geometry (1):
    g0: Circle CenterX=0 CenterY=0 CenterZ=0 NormalX=0 NormalY=0 NormalZ=1 AngleXU=0 Radius=4
  constraints (2):
    c: Coincident(g0,g-1)
    c: Diameter(g0) = 8
FEATURE [PartDesign::Pocket] Pocket
  BaseFeature = -> Revolution
  Length = 5
  Length2 = 100
  Midplane = true
  Placement = pos=(0,0,0) rot=(0.57735,0.57735,0.57735;2.0944rad)
  Profile = -> Sketch001
  Type = 1
FEATURE [Sketcher::SketchObject] Sketch002
  FullyConstrained = true
  MapMode = 5
  Support = -> [XY_Plane]
  sketch-geometry (1):
    g0: Circle CenterX=0 CenterY=8 CenterZ=0 NormalX=0 NormalY=0 NormalZ=1 AngleXU=0 Radius=1.5
  constraints (3):
    c: Diameter(g0) = 3
    c: Vertical(g0,g-1)
    c: DistanceY(g-1,g0) = 8
FEATURE [PartDesign::Hole] Hole
  BaseFeature = -> Pocket
  Depth = 10
  DepthType = 0
  Diameter = 3.4
  DrillForDepth = false
  DrillPoint = 1
  DrillPointAngle = 118
  HoleCutCountersinkAngle = 90
  HoleCutCustomValues = false
  HoleCutDepth = 3.4
  HoleCutDiameter = 6.1
  HoleCutType = 0
  ModelActualThread = false
  Placement = pos=(0,0,0) rot=(0.57735,0.57735,0.57735;2.0944rad)
  Profile = -> Sketch002
  Tapered = false
  TaperedAngle = 90
  ThreadAngle = 60
  ThreadClass = 0
  ThreadCutOffInner = 0.0541266
  ThreadCutOffOuter = 0.108253
  ThreadDirection = 0
  ThreadFit = 0
  ThreadPitch = 0.5
  ThreadSize = 9
  ThreadType = 1
  Threaded = false
FEATURE [PartDesign::PolarPattern] PolarPattern
  Angle = 360
  Axis = -> Sketch002 [N_Axis]
  BaseFeature = -> Hole
  Occurrences = 4
  Originals = -> [Hole]
  Placement = pos=(0,0,0) rot=(0.57735,0.57735,0.57735;2.0944rad)
FEATURE [PartDesign::CoordinateSystem] Local_CS  label="lcs_screw1"
  AttacherType = Attacher::AttachEngine3D
  AttachmentOffset = pos=(0,0,0) rot=(0,0,1;3.14159rad)
  MapMode = 11
  Placement = pos=(-8,0,-2e-15) rot=(0.707107,-0.707107,0;3.14159rad)
  Support = -> [PolarPattern]
FEATURE [PartDesign::CoordinateSystem] Local_CS001  label="lcs_nut_lead_screw"
  AttacherType = Attacher::AttachEngine3D
  AttachmentOffset = pos=(0,0,0) rot=(0,0,1;0.785398rad)
  MapMode = 11
  Placement = pos=(1.8e-15,-9e-16,-4) rot=(0.92388,-0.382683,0;3.14159rad)
  Support = -> [PolarPattern]
FEATURE [PartDesign::CoordinateSystem] Local_CS002
  AttacherType = Attacher::AttachEngine3D
  AttachmentOffset = pos=(0,0,0) rot=(0,0,1;0.785398rad)
  MapMode = 11
  Placement = pos=(-8.9e-15,-9.1e-15,0) rot=(0,0,1;2.35619rad)
  Support = -> [PolarPattern]
FEATURE [PartDesign::Body] Body
  Group = -> [Sketch,Revolution,Sketch001,Pocket,Sketch002,Hole,PolarPattern,Local_CS,Local_CS001,Local_CS002]
  Origin = -> Origin
  Tip = -> PolarPattern
---- part rod_threaded_8mm.FCStd = doc fcstd_d29657fa016d ----
FCSTD DOCUMENT  (FreeCAD 0.19R)
Label: rod_threaded_8mm
License: All rights reserved
LicenseURL: http://en.wikipedia.org/wiki/All_rights_reserved
objects: PartDesign::CoordinateSystem×2, Sketcher::SketchObject×1, PartDesign::Pad×1, PartDesign::Body×1
note: 6 computed .brp shape members not serialized (recipe doc carries the construction recipe); baked Part::Feature solids carry a one-line shape summary decoded from their .brp

FEATURE [Sketcher::SketchObject] Sketch
  FullyConstrained = true
  MapMode = 5
  Support = -> [XY_Plane]
  sketch-geometry (1):
    g0: Circle CenterX=0 CenterY=0 CenterZ=0 NormalX=0 NormalY=0 NormalZ=1 AngleXU=0 Radius=4
  constraints (2):
    c: Coincident(g0,g-1)
    c: Diameter(g0) = 8
FEATURE [PartDesign::Pad] Pad
  Direction = (1,1,1)
  Length = 450
  Length2 = 100
  Profile = -> Sketch
  Refine = true
  Type = 0
FEATURE [PartDesign::CoordinateSystem] Local_CS
  AttacherType = Attacher::AttachEngine3D
  MapMode = 11
  Placement = pos=(0,0,0) rot=(0,0,1;1.5708rad)
  Support = -> [Pad]
FEATURE [PartDesign::CoordinateSystem] Local_CS001
  AttacherType = Attacher::AttachEngine3D
  MapMode = 11
  Placement = pos=(0,0,450) rot=(0,0,1;1.5708rad)
  Support = -> [Pad]
FEATURE [PartDesign::Body] Body
  Group = -> [Sketch,Pad,Local_CS,Local_CS001]
  Origin = -> Origin
  Tip = -> Pad
---- part shaft_8mm.FCStd = doc fcstd_b43212a9ea34 ----
FCSTD DOCUMENT  (FreeCAD 0.19R)
Label: shaft_8mm
License: All rights reserved
LicenseURL: http://en.wikipedia.org/wiki/All_rights_reserved
objects: PartDesign::CoordinateSystem×2, Sketcher::SketchObject×1, PartDesign::Pad×1, PartDesign::Body×1
note: 6 computed .brp shape members not serialized (recipe doc carries the construction recipe); baked Part::Feature solids carry a one-line shape summary decoded from their .brp

FEATURE [Sketcher::SketchObject] Sketch
  FullyConstrained = true
  MapMode = 5
  Support = -> [XY_Plane]
  sketch-geometry (1):
    g0: Circle CenterX=0 CenterY=0 CenterZ=0 NormalX=0 NormalY=0 NormalZ=1 AngleXU=0 Radius=4
  constraints (2):
    c: Coincident(g0,g-1)
    c: Diameter(g0) = 8
FEATURE [PartDesign::Pad] Pad
  Direction = (1,1,1)
  Length = 400
  Length2 = 100
  Profile = -> Sketch
  Refine = true
  Type = 0
FEATURE [PartDesign::CoordinateSystem] Local_CS
  AttacherType = Attacher::AttachEngine3D
  MapMode = 11
  Placement = pos=(0,0,400) rot=(0,0,1;1.5708rad)
  Support = -> [Pad]
FEATURE [PartDesign::CoordinateSystem] Local_CS001
  AttacherType = Attacher::AttachEngine3D
  MapMode = 11
  Placement = pos=(0,0,0) rot=(0,0,1;1.5708rad)
  Support = -> [Pad]
FEATURE [PartDesign::Body] Body
  Group = -> [Sketch,Pad,Local_CS,Local_CS001]
  Origin = -> Origin
  Tip = -> Pad
---- part support_shaft_horiz_8mm.FCStd = doc fcstd_dea334952a8f ----
FCSTD DOCUMENT  (FreeCAD 0.19R)
Label: support_shaft_horiz_8mm
License: All rights reserved
LicenseURL: http://en.wikipedia.org/wiki/All_rights_reserved
objects: PartDesign::CoordinateSystem×6, Sketcher::SketchObject×3, PartDesign::Pad×2, PartDesign::Pocket×1, PartDesign::Body×1
note: 16 computed .brp shape members not serialized (recipe doc carries the construction recipe); baked Part::Feature solids carry a one-line shape summary decoded from their .brp

FEATURE [Sketcher::SketchObject] Sketch
  FullyConstrained = true
  MapMode = 5
  Support = -> [XY_Plane]
  sketch-geometry (14):
    g0: Circle CenterX=0 CenterY=0 CenterZ=0 NormalX=0 NormalY=0 NormalZ=1 AngleXU=0 Radius=4
    g1: ArcOfCircle CenterX=16.76 CenterY=0 CenterZ=0 NormalX=0 NormalY=0 NormalZ=1 AngleXU=0 Radius=5 StartAngle=5.14326 EndAngle=7.42311
    g2: ArcOfCircle CenterX=-16.76 CenterY=0 CenterZ=0 NormalX=0 NormalY=0 NormalZ=1 AngleXU=0 Radius=5 StartAngle=2.00167 EndAngle=4.28151
    g3: GeomPoint X=-21.76 Y=0 Z=0
    g4: LineSegment StartX=5.01193 StartY=10.9032 StartZ=0 EndX=18.8483 EndY=4.54301 EndZ=0
    g5: LineSegment StartX=-18.8483 StartY=4.54301 StartZ=0 EndX=-5.01193 EndY=10.9032 EndZ=0
    g6: ArcOfCircle CenterX=0 CenterY=0 CenterZ=0 NormalX=0 NormalY=0 NormalZ=1 AngleXU=0 Radius=12 StartAngle=1.13993 EndAngle=2.00167
    g7: ArcOfCircle CenterX=0 CenterY=0 CenterZ=0 NormalX=0 NormalY=0 NormalZ=1 AngleXU=0 Radius=12 StartAngle=4.28152 EndAngle=5.14326
    g8: GeomPoint X=21.76 Y=0 Z=0
    g9: Circle CenterX=-16 CenterY=0 CenterZ=0 NormalX=0 NormalY=0 NormalZ=1 AngleXU=0 Radius=2.75
    g10: Circle CenterX=16 CenterY=0 CenterZ=0 NormalX=0 NormalY=0 NormalZ=1 AngleXU=0 Radius=2.75
    g11: Circle CenterX=0 CenterY=0 CenterZ=0 NormalX=0 NormalY=0 NormalZ=1 AngleXU=0 Radius=12
    g12: LineSegment StartX=-18.8483 StartY=-4.543 StartZ=0 EndX=-5.01194 EndY=-10.9032 EndZ=0
    g13: LineSegment StartX=5.01192 StartY=-10.9032 StartZ=0 EndX=18.8483 EndY=-4.54301 EndZ=0
  constraints (34):
    c: Diameter(g0) = 8
    c: Equal(g2,g1)
    c: PointOnObject(g3,g2)
    c: Tangent(g6,g4) = 1.5708
    c: Tangent(g2,g5) = 1.5708
    c: Tangent(g1,g4) = 1.5708
    c: Coincident(g6,g0)
    c: Horizontal(g3,g0)
    c: Tangent(g6,g5) = 1.5708
    c: Coincident(g7,g0)
    c: Horizontal(g0,g8)
    c: PointOnObject(g8,g1)
    c: DistanceX(g3,g8) = 43.52
    c: Symmetric(g9,g10,g0)
    c: Diameter(g9) = 5.5
    c: Horizontal(g9,g0)
    c: DistanceX(g9,g10) = 32
    c: Coincident(g0,g11)
    c: Diameter(g11) = 24
    c: PointOnObject(g4,g11)
    c: Coincident(g0,g-1)
    c: PointOnObject(g7,g11)
    c: Coincident(g12,g2)
    c: Coincident(g12,g7)
    c: Coincident(g13,g7)
    c: Coincident(g13,g1)
    c: Tangent(g1,g13)
    c: Tangent(g12,g2)
    c: Tangent(g7,g12)
    c: Symmetric(g2,g1,g0)
    c: Horizontal(g1,g0)
    c: Diameter(g1) = 10
    c: Tangent(g13,g7)
    c: Equal(g10,g9)
FEATURE [PartDesign::Pad] Pad
  Direction = (1,1,1)
  Length = 10
  Length2 = 100
  Midplane = true
  Profile = -> Sketch
  Type = 0
FEATURE [Sketcher::SketchObject] Sketch001
  FullyConstrained = true
  MapMode = 5
  Placement = pos=(0,0,0) rot=(0.57735,0.57735,0.57735;2.0944rad)
  Support = -> [YZ_Plane]
  sketch-geometry (1):
    g0: Circle CenterX=-8.63 CenterY=0 CenterZ=0 NormalX=0 NormalY=0 NormalZ=1 AngleXU=0 Radius=3
  constraints (3):
    c: PointOnObject(g0,g-1)
    c: Radius(g0) = 3
    c: DistanceX(g0,g-1) = 8.63
FEATURE [PartDesign::Pad] Pad001
  BaseFeature = -> Pad
  Direction = (1,1,1)
  Length = 30
  Length2 = 100
  Midplane = true
  Profile = -> Sketch001
  Type = 0
FEATURE [Sketcher::SketchObject] Sketch002
  FullyConstrained = true
  MapMode = 5
  Placement = pos=(0,0,0) rot=(1,0,0;1.5708rad)
  Support = -> [XZ_Plane]
  sketch-geometry (4):
    g0: LineSegment StartX=-0.5 StartY=-19.575 StartZ=0 EndX=0.5 EndY=-19.575 EndZ=0
    g1: LineSegment StartX=0.5 StartY=-19.575 StartZ=0 EndX=0.5 EndY=19.575 EndZ=0
    g2: LineSegment StartX=0.5 StartY=19.575 StartZ=0 EndX=-0.5 EndY=19.575 EndZ=0
    g3: LineSegment StartX=-0.5 StartY=19.575 StartZ=0 EndX=-0.5 EndY=-19.575 EndZ=0
  constraints (11):
    c: Coincident(g0,g1)
    c: Coincident(g1,g2)
    c: Coincident(g2,g3)
    c: Coincident(g3,g0)
    c: Horizontal(g0)
    c: Horizontal(g2)
    c: Vertical(g1)
    c: Vertical(g3)
    c: Symmetric(g2,g0,g-1)
    c: DistanceX(g2,g2) = 1
    c: DistanceY(g1,g1) = 39.15
FEATURE [PartDesign::Pocket] Pocket
  BaseFeature = -> Pad001
  Length = 5
  Length2 = 100
  Profile = -> Sketch002
  Reversed = true
  Type = 1
FEATURE [PartDesign::CoordinateSystem] Local_CS  label="local_left"
  AttacherType = Attacher::AttachEngine3D
  MapMode = 11
  Placement = pos=(-16,0,5) rot=(0,0,1;1.5708rad)
  Support = -> [Pad]
FEATURE [PartDesign::CoordinateSystem] Local_CS001  label="local_right"
  AttacherType = Attacher::AttachEngine3D
  MapMode = 11
  Placement = pos=(0,0,-5) rot=(0,0,1;1.5708rad)
  Support = -> [Pad]
FEATURE [PartDesign::CoordinateSystem] Local_CS002
  AttacherType = Attacher::AttachEngine3D
  MapMode = 11
  Placement = pos=(16,0,5) rot=(0,0,1;1.5708rad)
  Support = -> [Pad]
FEATURE [PartDesign::CoordinateSystem] Local_CS003
  AttacherType = Attacher::AttachEngine3D
  MapMode = 11
  Placement = pos=(-16,0,-5) rot=(0,0,1;1.5708rad)
  Support = -> [Pad]
FEATURE [PartDesign::CoordinateSystem] Local_CS004
  AttacherType = Attacher::AttachEngine3D
  MapMode = 11
  Placement = pos=(16,0,-5) rot=(0,0,1;1.5708rad)
  Support = -> [Pad]
FEATURE [PartDesign::CoordinateSystem] Local_CS005
  AttacherType = Attacher::AttachEngine3D
  MapMode = 11
  Placement = pos=(0,0,5) rot=(0,0,1;1.5708rad)
  Support = -> [Pad]
FEATURE [PartDesign::Body] Body
  Group = -> [Sketch,Pad,Sketch001,Local_CS,Local_CS001,Local_CS002,Local_CS003,Local_CS004,Local_CS005,Pad001,Sketch002,Pocket]
  Origin = -> Origin
  Tip = -> Pad
